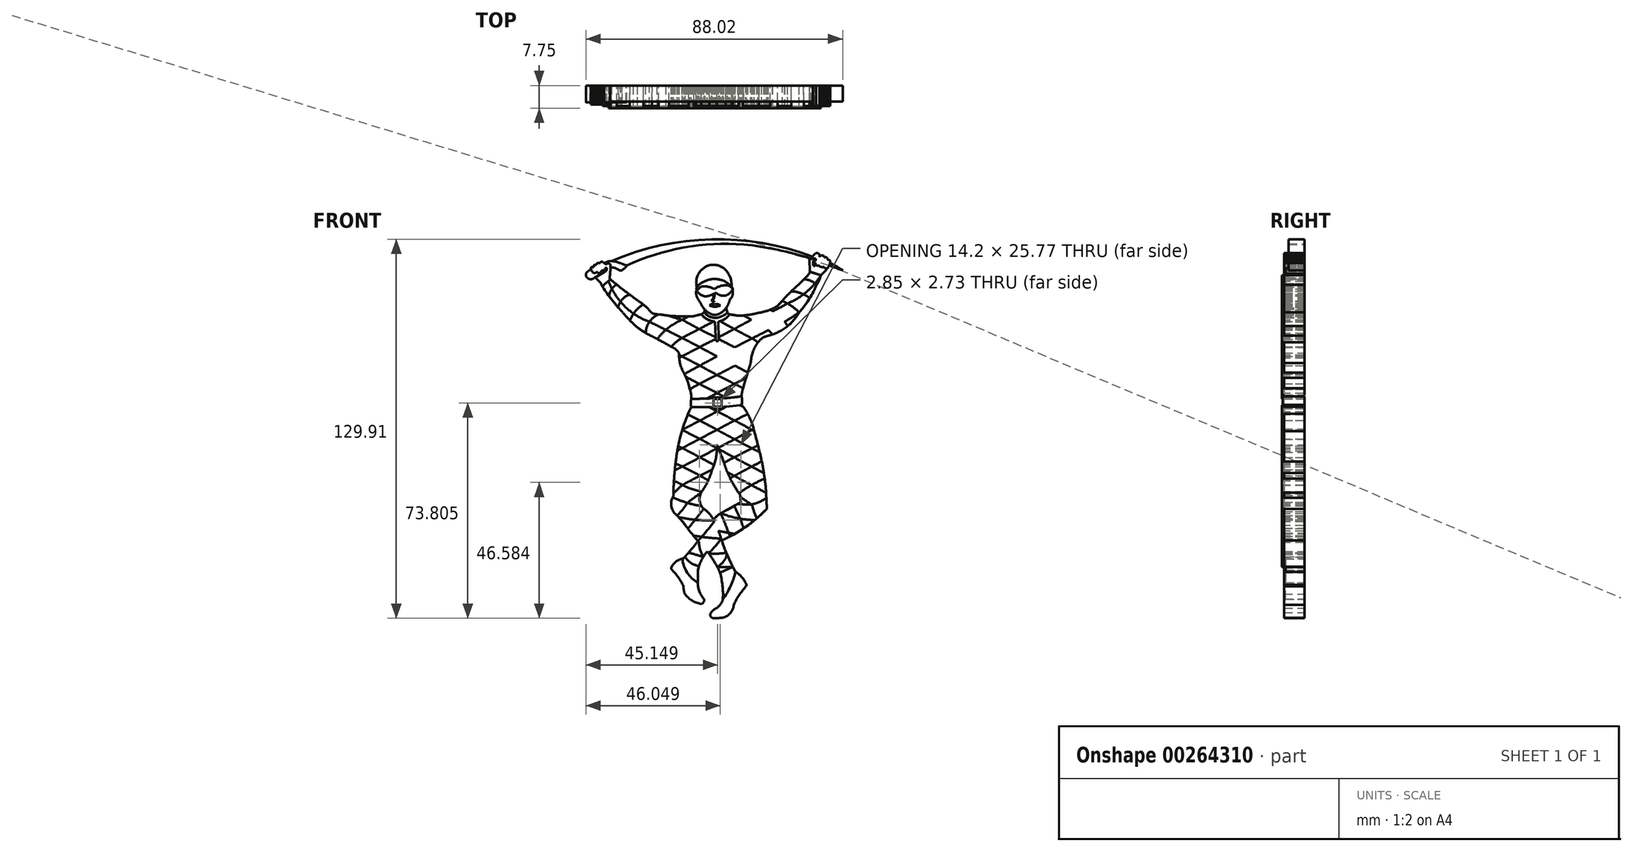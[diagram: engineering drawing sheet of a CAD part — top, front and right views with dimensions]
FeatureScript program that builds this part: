
annotation { "Feature Type Name" : "Feature", "Feature Type Description" : "" }
export const myFeature = defineFeature(function(context is Context, id is Id, definition is map)
    precondition{}
    {
        {
            var Q0;
            Q0=qCreatedBy(makeId("Front.planeOp"),FACE);
            var sketch = newSketch(context, id + "F0", { "sketchPlane" : qUnion([Q0])});
            skArc(sketch, "E0", {"start": v(-36.37, 62.76) * mm, "mid": v(-36.1, 65.18) * mm, "end": v(-36.02, 67.61) * mm});
            skLineSegment(sketch, "E1", {"start": v(-36.02, 67.61) * mm, "end": v(-36.67, 68.1) * mm});
            skArc(sketch, "E2", {"start": v(-36.67, 68.1) * mm, "mid": v(-37.17, 67.96) * mm, "end": v(-37.6, 67.68) * mm});
            skArc(sketch, "E3", {"start": v(-37.6, 67.68) * mm, "mid": v(-38.2, 68.15) * mm, "end": v(-38.83, 68.59) * mm});
            skArc(sketch, "E4", {"start": v(-38.83, 68.59) * mm, "mid": v(-39.14, 68.59) * mm, "end": v(-39.4, 68.45) * mm});
            skArc(sketch, "E5", {"start": v(-39.4, 68.45) * mm, "mid": v(-39.54, 68.3) * mm, "end": v(-39.58, 68.1) * mm});
            skArc(sketch, "E6", {"start": v(-39.58, 68.1) * mm, "mid": v(-39.84, 68.17) * mm, "end": v(-40.1, 68.2) * mm});
            skArc(sketch, "E7", {"start": v(-40.1, 68.2) * mm, "mid": v(-40.37, 68.18) * mm, "end": v(-40.6, 68.05) * mm});
            skArc(sketch, "E8", {"start": v(-40.6, 68.05) * mm, "mid": v(-40.8, 67.83) * mm, "end": v(-40.9, 67.56) * mm});
            skArc(sketch, "E9", {"start": v(-41.46, 67.56) * mm, "mid": v(-41.64, 67.48) * mm, "end": v(-41.77, 67.32) * mm});
            skArc(sketch, "E10", {"start": v(-41.77, 67.32) * mm, "mid": v(-41.81, 67.07) * mm, "end": v(-41.77, 66.82) * mm});
            skArc(sketch, "E11", {"start": v(-40.9, 67.56) * mm, "mid": v(-41.18, 67.58) * mm, "end": v(-41.46, 67.56) * mm});
            skArc(sketch, "E12", {"start": v(-41.77, 66.82) * mm, "mid": v(-42.13, 66.8) * mm, "end": v(-42.5, 66.74) * mm});
            skArc(sketch, "E13", {"start": v(-42.5, 66.74) * mm, "mid": v(-42.65, 66.64) * mm, "end": v(-42.73, 66.47) * mm});
            skArc(sketch, "E14", {"start": v(-42.73, 66.47) * mm, "mid": v(-42.46, 65.5) * mm, "end": v(-41.77, 64.76) * mm});
            skArc(sketch, "E15", {"start": v(-41.77, 64.76) * mm, "mid": v(-41.15, 64.8) * mm, "end": v(-40.64, 65.13) * mm});
            skArc(sketch, "E16", {"start": v(-40.64, 65.13) * mm, "mid": v(-40.38, 64.82) * mm, "end": v(-39.99, 64.68) * mm});
            skArc(sketch, "E17", {"start": v(-39.99, 64.68) * mm, "mid": v(-39.6, 64.72) * mm, "end": v(-39.3, 64.98) * mm});
            skArc(sketch, "E18", {"start": v(-39.3, 64.98) * mm, "mid": v(-39.18, 65.24) * mm, "end": v(-39.15, 65.53) * mm});
            skArc(sketch, "E19", {"start": v(-38.55, 65.59) * mm, "mid": v(-38.85, 65.56) * mm, "end": v(-39.15, 65.53) * mm});
            skArc(sketch, "E20", {"start": v(-38.55, 65.59) * mm, "mid": v(-38.33, 65.65) * mm, "end": v(-38.15, 65.79) * mm});
            skArc(sketch, "E21", {"start": v(-38.15, 65.79) * mm, "mid": v(-37.9, 66.12) * mm, "end": v(-37.76, 66.5) * mm});
            skArc(sketch, "E22", {"start": v(-37.28, 66.5) * mm, "mid": v(-37.52, 66.52) * mm, "end": v(-37.76, 66.5) * mm});
            skArc(sketch, "E23", {"start": v(-38.34, 65) * mm, "mid": v(-37.5, 65.52) * mm, "end": v(-37.28, 66.5) * mm});
            skLineSegment(sketch, "E24", {"start": v(-38.34, 65) * mm, "end": v(-41.2, 63.26) * mm});
            skLineSegment(sketch, "E25", {"start": v(-41.2, 63.26) * mm, "end": v(-39.25, 61.15) * mm});
            skArc(sketch, "E26", {"start": v(-39.25, 61.15) * mm, "mid": v(-39.04, 60.49) * mm, "end": v(-38.65, 59.91) * mm});
            skArc(sketch, "E27", {"start": v(-38.14, 60.8) * mm, "mid": v(-38.44, 60.38) * mm, "end": v(-38.65, 59.91) * mm});
            skLineSegment(sketch, "E28", {"start": v(-38.14, 60.8) * mm, "end": v(-36.03, 62.5) * mm});
            skArc(sketch, "E29", {"start": v(-36.03, 62.5) * mm, "mid": v(-36.17, 62.67) * mm, "end": v(-36.37, 62.76) * mm});
            skLineSegment(sketch, "E30", {"start": v(-3.7, 52.22) * mm, "end": v(-3.93, 51.3) * mm});
            skArc(sketch, "E31", {"start": v(-3.93, 51.3) * mm, "mid": v(-2.81, 50.2) * mm, "end": v(-1.39, 49.54) * mm});
            skArc(sketch, "E32", {"start": v(-1.39, 49.54) * mm, "mid": v(0.04, 49.34) * mm, "end": v(1.46, 49.64) * mm});
            skArc(sketch, "E33", {"start": v(1.46, 49.64) * mm, "mid": v(2.82, 50.24) * mm, "end": v(4.06, 51.06) * mm});
            skLineSegment(sketch, "E34", {"start": v(3.58, 52.8) * mm, "end": v(4.06, 51.06) * mm});
            skArc(sketch, "E35", {"start": v(-3.7, 52.22) * mm, "mid": v(-2.6, 51.2) * mm, "end": v(-1.23, 50.54) * mm});
            skArc(sketch, "E36", {"start": v(-1.23, 50.54) * mm, "mid": v(-0.11, 50.37) * mm, "end": v(0.99, 50.62) * mm});
            skArc(sketch, "E37", {"start": v(0.99, 50.62) * mm, "mid": v(2.44, 51.52) * mm, "end": v(3.58, 52.8) * mm});
            skLineSegment(sketch, "E38", {"start": v(32.12, 69.37) * mm, "end": v(32.24, 65.2) * mm});
            skLineSegment(sketch, "E39", {"start": v(32.24, 65.2) * mm, "end": v(36.08, 63.91) * mm});
            skArc(sketch, "E40", {"start": v(36.7, 64.53) * mm, "mid": v(36.38, 64.23) * mm, "end": v(36.08, 63.91) * mm});
            skArc(sketch, "E41", {"start": v(36.7, 64.53) * mm, "mid": v(37.54, 65.4) * mm, "end": v(38.3, 66.32) * mm});
            skArc(sketch, "E42", {"start": v(37.73, 66.32) * mm, "mid": v(38.02, 66.3) * mm, "end": v(38.3, 66.32) * mm});
            skArc(sketch, "E43", {"start": v(37.06, 66.85) * mm, "mid": v(37.33, 66.5) * mm, "end": v(37.73, 66.32) * mm});
            skArc(sketch, "E44", {"start": v(35.98, 66.85) * mm, "mid": v(36.52, 66.8) * mm, "end": v(37.06, 66.85) * mm});
            skArc(sketch, "E45", {"start": v(35.56, 67.22) * mm, "mid": v(35.72, 66.98) * mm, "end": v(35.98, 66.85) * mm});
            skArc(sketch, "E46", {"start": v(34.59, 67.38) * mm, "mid": v(35.06, 67.24) * mm, "end": v(35.56, 67.22) * mm});
            skArc(sketch, "E47", {"start": v(34.17, 67.88) * mm, "mid": v(34.32, 67.58) * mm, "end": v(34.59, 67.38) * mm});
            skArc(sketch, "E48", {"start": v(34.17, 68.32) * mm, "mid": v(34.14, 68.1) * mm, "end": v(34.17, 67.88) * mm});
            skArc(sketch, "E49", {"start": v(32.75, 69.71) * mm, "mid": v(32.4, 69.6) * mm, "end": v(32.12, 69.37) * mm});
            skLineSegment(sketch, "E50", {"start": v(32.75, 69.71) * mm, "end": v(34.26, 69.71) * mm});
            skArc(sketch, "E51", {"start": v(34.26, 69.18) * mm, "mid": v(34.35, 69.45) * mm, "end": v(34.26, 69.71) * mm});
            skArc(sketch, "E52", {"start": v(33.47, 68.74) * mm, "mid": v(33.91, 68.89) * mm, "end": v(34.26, 69.18) * mm});
            skLineSegment(sketch, "E53", {"start": v(33.47, 68.74) * mm, "end": v(33.47, 67.5) * mm});
            skArc(sketch, "E54", {"start": v(33.47, 67.5) * mm, "mid": v(33.54, 67.3) * mm, "end": v(33.72, 67.2) * mm});
            skArc(sketch, "E55", {"start": v(33.72, 67.2) * mm, "mid": v(33.9, 67.2) * mm, "end": v(34.01, 67.34) * mm});
            skArc(sketch, "E56", {"start": v(34.01, 67.34) * mm, "mid": v(33.99, 67.52) * mm, "end": v(33.88, 67.66) * mm});
            skArc(sketch, "E57", {"start": v(33.88, 68.3) * mm, "mid": v(33.84, 67.98) * mm, "end": v(33.88, 67.66) * mm});
            skArc(sketch, "E58", {"start": v(34.17, 68.32) * mm, "mid": v(34.02, 68.32) * mm, "end": v(33.88, 68.3) * mm});
            skArc(sketch, "E59", {"start": v(-10.4, -32.58) * mm, "mid": v(-8.42, -34.73) * mm, "end": v(-5.68, -35.77) * mm});
            skArc(sketch, "E60", {"start": v(-11.4, -33.28) * mm, "mid": v(-9.76, -38) * mm, "end": v(-6.12, -41.43) * mm});
            skArc(sketch, "E61", {"start": v(-6.12, -41.43) * mm, "mid": v(-6.03, -39.3) * mm, "end": v(-6.04, -37.17) * mm});
            skLineSegment(sketch, "E62", {"start": v(-6.04, -37.17) * mm, "end": v(-5.68, -35.77) * mm});
            skLineSegment(sketch, "E63", {"start": v(-11.4, -33.28) * mm, "end": v(-10.4, -32.58) * mm});
            skArc(sketch, "E64", {"start": v(2.49, -47.2) * mm, "mid": v(2.36, -42.53) * mm, "end": v(1.48, -37.94) * mm});
            skArc(sketch, "E65", {"start": v(2.49, -47.2) * mm, "mid": v(5.15, -42.7) * mm, "end": v(6.82, -37.74) * mm});
            skLineSegment(sketch, "E66", {"start": v(1.48, -37.94) * mm, "end": v(5.96, -36.05) * mm});
            skLineSegment(sketch, "E67", {"start": v(5.96, -36.05) * mm, "end": v(6.82, -37.74) * mm});
            skSolve(sketch);
        }
        {
            var Q0;
            Q0=qCreatedBy(makeId("Front.planeOp"),FACE);
            var sketch = newSketch(context, id + "F1", { "sketchPlane" : qUnion([Q0])});
            skArc(sketch, "E68", {"start": v(34.17, 68.32) * mm, "mid": v(34.14, 68.1) * mm, "end": v(34.18, 67.88) * mm});
            skArc(sketch, "E69", {"start": v(34.18, 67.88) * mm, "mid": v(34.32, 67.58) * mm, "end": v(34.59, 67.39) * mm});
            skArc(sketch, "E70", {"start": v(34.59, 67.39) * mm, "mid": v(35.06, 67.25) * mm, "end": v(35.55, 67.23) * mm});
            skArc(sketch, "E71", {"start": v(35.55, 67.23) * mm, "mid": v(35.72, 66.98) * mm, "end": v(35.99, 66.85) * mm});
            skArc(sketch, "E72", {"start": v(35.99, 66.85) * mm, "mid": v(36.52, 66.8) * mm, "end": v(37.06, 66.85) * mm});
            skArc(sketch, "E73", {"start": v(37.06, 66.85) * mm, "mid": v(37.33, 66.5) * mm, "end": v(37.73, 66.32) * mm});
            skArc(sketch, "E74", {"start": v(37.73, 66.32) * mm, "mid": v(38.02, 66.3) * mm, "end": v(38.3, 66.32) * mm});
            skArc(sketch, "E75", {"start": v(33.48, 68.47) * mm, "mid": v(33.8, 68.33) * mm, "end": v(34.17, 68.32) * mm});
            skArc(sketch, "E76", {"start": v(38.3, 66.32) * mm, "mid": v(38.86, 67.2) * mm, "end": v(39.2, 68.2) * mm});
            skArc(sketch, "E77", {"start": v(39.2, 68.2) * mm, "mid": v(39.27, 68.59) * mm, "end": v(39.2, 68.98) * mm});
            skArc(sketch, "E78", {"start": v(39.2, 68.98) * mm, "mid": v(39.02, 69.14) * mm, "end": v(38.8, 69.25) * mm});
            skArc(sketch, "E79", {"start": v(38.8, 69.25) * mm, "mid": v(38.55, 69.29) * mm, "end": v(38.3, 69.25) * mm});
            skArc(sketch, "E80", {"start": v(38.3, 69.25) * mm, "mid": v(38.35, 69.5) * mm, "end": v(38.3, 69.76) * mm});
            skArc(sketch, "E81", {"start": v(38.3, 69.76) * mm, "mid": v(38.14, 70) * mm, "end": v(37.9, 70.14) * mm});
            skArc(sketch, "E82", {"start": v(37.9, 70.14) * mm, "mid": v(37.59, 70.14) * mm, "end": v(37.28, 70.06) * mm});
            skArc(sketch, "E83", {"start": v(34.46, 71.56) * mm, "mid": v(33.88, 71.14) * mm, "end": v(33.43, 70.59) * mm});
            skArc(sketch, "E84", {"start": v(35.55, 71.17) * mm, "mid": v(35.06, 71.53) * mm, "end": v(34.46, 71.56) * mm});
            skArc(sketch, "E85", {"start": v(33.43, 70.59) * mm, "mid": v(33.12, 70.16) * mm, "end": v(32.87, 69.71) * mm});
            skArc(sketch, "E86", {"start": v(34.27, 69.18) * mm, "mid": v(34.35, 69.45) * mm, "end": v(34.26, 69.71) * mm});
            skArc(sketch, "E87", {"start": v(33.47, 68.75) * mm, "mid": v(33.91, 68.89) * mm, "end": v(34.27, 69.18) * mm});
            skLineSegment(sketch, "E88", {"start": v(33.47, 68.75) * mm, "end": v(33.48, 68.47) * mm});
            skLineSegment(sketch, "E89", {"start": v(32.87, 69.71) * mm, "end": v(34.26, 69.71) * mm});
            skArc(sketch, "E90", {"start": v(35.55, 70.31) * mm, "mid": v(35.6, 70.74) * mm, "end": v(35.55, 71.17) * mm});
            skArc(sketch, "E91", {"start": v(36.26, 70.76) * mm, "mid": v(35.88, 70.59) * mm, "end": v(35.55, 70.31) * mm});
            skArc(sketch, "E92", {"start": v(37.11, 70.59) * mm, "mid": v(36.7, 70.74) * mm, "end": v(36.26, 70.76) * mm});
            skArc(sketch, "E93", {"start": v(37.28, 70.06) * mm, "mid": v(37.25, 70.34) * mm, "end": v(37.11, 70.59) * mm});
            skArc(sketch, "E94", {"start": v(-3.7, 52.23) * mm, "mid": v(-2.6, 51.2) * mm, "end": v(-1.23, 50.54) * mm});
            skArc(sketch, "E95", {"start": v(-1.23, 50.54) * mm, "mid": v(-0.11, 50.38) * mm, "end": v(1, 50.62) * mm});
            skArc(sketch, "E96", {"start": v(1, 50.62) * mm, "mid": v(2.44, 51.52) * mm, "end": v(3.57, 52.8) * mm});
            skArc(sketch, "E97", {"start": v(3.57, 52.8) * mm, "mid": v(4.44, 54.19) * mm, "end": v(4.91, 55.77) * mm});
            skArc(sketch, "E98", {"start": v(4.91, 55.77) * mm, "mid": v(5.55, 56.45) * mm, "end": v(5.85, 57.33) * mm});
            skArc(sketch, "E99", {"start": v(5.85, 57.33) * mm, "mid": v(5.91, 58.44) * mm, "end": v(5.85, 59.54) * mm});
            skArc(sketch, "E100", {"start": v(5.85, 59.54) * mm, "mid": v(5.68, 59.75) * mm, "end": v(5.46, 59.9) * mm});
            skArc(sketch, "E101", {"start": v(5.46, 59.9) * mm, "mid": v(3.62, 61.6) * mm, "end": v(1.28, 62.5) * mm});
            skArc(sketch, "E102", {"start": v(1.28, 62.5) * mm, "mid": v(-0.42, 62.68) * mm, "end": v(-2.12, 62.5) * mm});
            skArc(sketch, "E103", {"start": v(-2.12, 62.5) * mm, "mid": v(-4.49, 61.54) * mm, "end": v(-6.45, 59.9) * mm});
            skArc(sketch, "E104", {"start": v(-6.45, 59.9) * mm, "mid": v(-6.53, 59.3) * mm, "end": v(-6.45, 58.69) * mm});
            skArc(sketch, "E105", {"start": v(-6.45, 58.69) * mm, "mid": v(-6.62, 58.63) * mm, "end": v(-6.73, 58.5) * mm});
            skArc(sketch, "E106", {"start": v(-6.73, 58.5) * mm, "mid": v(-6.4, 56.54) * mm, "end": v(-5.38, 54.84) * mm});
            skArc(sketch, "E107", {"start": v(-5.38, 54.84) * mm, "mid": v(-4.67, 53.45) * mm, "end": v(-3.7, 52.23) * mm});
            skSolve(sketch);
        }
        {
            var Q0;
            Q0=qCreatedBy(makeId("Front.planeOp"),FACE);
            var sketch = newSketch(context, id + "F2", { "sketchPlane" : qUnion([Q0])});
            skArc(sketch, "E108", {"start": v(-38.15, 60.8) * mm, "mid": v(-38.45, 60.39) * mm, "end": v(-38.65, 59.92) * mm});
            skLineSegment(sketch, "E109", {"start": v(-38.15, 60.8) * mm, "end": v(-36, 62.53) * mm});
            skArc(sketch, "E110", {"start": v(-36, 62.53) * mm, "mid": v(-30.5, 58.1) * mm, "end": v(-24.76, 53.97) * mm});
            skArc(sketch, "E111", {"start": v(-21.76, 50.88) * mm, "mid": v(-23.2, 52.48) * mm, "end": v(-24.76, 53.97) * mm});
            skArc(sketch, "E112", {"start": v(-21.76, 50.88) * mm, "mid": v(-14.63, 49.98) * mm, "end": v(-7.45, 49.93) * mm});
            skArc(sketch, "E113", {"start": v(-4.86, 50.59) * mm, "mid": v(-6.16, 50.28) * mm, "end": v(-7.45, 49.93) * mm});
            skArc(sketch, "E114", {"start": v(-4.86, 50.59) * mm, "mid": v(-4.37, 50.92) * mm, "end": v(-3.92, 51.3) * mm});
            skArc(sketch, "E115", {"start": v(-3.92, 51.3) * mm, "mid": v(-2.82, 50.2) * mm, "end": v(-1.4, 49.56) * mm});
            skArc(sketch, "E116", {"start": v(-1.4, 49.56) * mm, "mid": v(0.04, 49.34) * mm, "end": v(1.46, 49.64) * mm});
            skArc(sketch, "E117", {"start": v(1.46, 49.64) * mm, "mid": v(2.82, 50.24) * mm, "end": v(4.06, 51.06) * mm});
            skArc(sketch, "E118", {"start": v(4.06, 51.06) * mm, "mid": v(4.28, 50.8) * mm, "end": v(4.53, 50.59) * mm});
            skArc(sketch, "E119", {"start": v(14.9, 51.11) * mm, "mid": v(18.2, 51.95) * mm, "end": v(21.24, 53.44) * mm});
            skArc(sketch, "E120", {"start": v(25.94, 58.47) * mm, "mid": v(23.55, 55.99) * mm, "end": v(21.24, 53.44) * mm});
            skArc(sketch, "E121", {"start": v(25.94, 58.47) * mm, "mid": v(29.17, 61.45) * mm, "end": v(32.18, 64.66) * mm});
            skArc(sketch, "E122", {"start": v(32.18, 64.66) * mm, "mid": v(32.24, 64.92) * mm, "end": v(32.24, 65.2) * mm});
            skArc(sketch, "E123", {"start": v(34.57, 60.7) * mm, "mid": v(35.48, 62.23) * mm, "end": v(36.07, 63.91) * mm});
            skArc(sketch, "E124", {"start": v(28.62, 51.25) * mm, "mid": v(32.02, 55.7) * mm, "end": v(34.57, 60.7) * mm});
            skArc(sketch, "E125", {"start": v(24.7, 46.53) * mm, "mid": v(26.87, 48.72) * mm, "end": v(28.62, 51.25) * mm});
            skArc(sketch, "E126", {"start": v(18.04, 43.23) * mm, "mid": v(21.55, 44.52) * mm, "end": v(24.7, 46.53) * mm});
            skArc(sketch, "E127", {"start": v(18.04, 43.23) * mm, "mid": v(16.08, 42.44) * mm, "end": v(14.53, 41) * mm});
            skArc(sketch, "E128", {"start": v(14.53, 41) * mm, "mid": v(12.75, 37.6) * mm, "end": v(12.02, 33.84) * mm});
            skArc(sketch, "E129", {"start": v(12.02, 33.84) * mm, "mid": v(10.66, 29.55) * mm, "end": v(9.44, 25.23) * mm});
            skLineSegment(sketch, "E130", {"start": v(2.72, 21.75) * mm, "end": v(2.72, 22.1) * mm});
            skLineSegment(sketch, "E131", {"start": v(2.72, 22.1) * mm, "end": v(-1.38, 22.1) * mm});
            skLineSegment(sketch, "E132", {"start": v(-1.38, 22.1) * mm, "end": v(-1.38, 21.75) * mm});
            skArc(sketch, "E133", {"start": v(-8.35, 21.5) * mm, "mid": v(-4.86, 21.55) * mm, "end": v(-1.38, 21.75) * mm});
            skArc(sketch, "E134", {"start": v(-8.37, 18.79) * mm, "mid": v(-4.87, 18.69) * mm, "end": v(-1.38, 18.82) * mm});
            skLineSegment(sketch, "E135", {"start": v(-1.38, 18.82) * mm, "end": v(-1.38, 18.28) * mm});
            skLineSegment(sketch, "E136", {"start": v(-1.38, 18.28) * mm, "end": v(2.72, 18.28) * mm});
            skLineSegment(sketch, "E137", {"start": v(2.72, 18.28) * mm, "end": v(2.72, 18.82) * mm});
            skArc(sketch, "E138", {"start": v(2.72, 18.82) * mm, "mid": v(5.83, 19.1) * mm, "end": v(8.92, 19.51) * mm});
            skArc(sketch, "E139", {"start": v(9.44, 25.23) * mm, "mid": v(9.05, 23.86) * mm, "end": v(8.92, 22.43) * mm});
            skArc(sketch, "E140", {"start": v(2.72, 21.75) * mm, "mid": v(5.83, 22) * mm, "end": v(8.92, 22.43) * mm});
            skArc(sketch, "E141", {"start": v(-8.35, 21.5) * mm, "mid": v(-8.4, 23.22) * mm, "end": v(-8.85, 24.9) * mm});
            skArc(sketch, "E142", {"start": v(-8.85, 24.9) * mm, "mid": v(-9.58, 27.56) * mm, "end": v(-10.7, 30.1) * mm});
            skArc(sketch, "E143", {"start": v(-12.5, 37.25) * mm, "mid": v(-12.12, 33.54) * mm, "end": v(-10.7, 30.1) * mm});
            skArc(sketch, "E144", {"start": v(-12.5, 37.25) * mm, "mid": v(-13.65, 38.51) * mm, "end": v(-15.1, 39.43) * mm});
            skArc(sketch, "E145", {"start": v(-15.1, 39.43) * mm, "mid": v(-18.37, 41.25) * mm, "end": v(-21.7, 42.97) * mm});
            skArc(sketch, "E146", {"start": v(-26.74, 46.02) * mm, "mid": v(-24.3, 44.37) * mm, "end": v(-21.7, 42.97) * mm});
            skArc(sketch, "E147", {"start": v(-32.1, 51.5) * mm, "mid": v(-29.54, 48.64) * mm, "end": v(-26.74, 46.02) * mm});
            skArc(sketch, "E148", {"start": v(-38.65, 59.92) * mm, "mid": v(-35.58, 55.55) * mm, "end": v(-32.1, 51.5) * mm});
            skArc(sketch, "E149", {"start": v(7.97, 50.06) * mm, "mid": v(6.25, 50.35) * mm, "end": v(4.53, 50.59) * mm});
            skArc(sketch, "E150", {"start": v(7.97, 50.06) * mm, "mid": v(11.47, 50.4) * mm, "end": v(14.9, 51.11) * mm});
            skArc(sketch, "E151", {"start": v(-8.37, 18.79) * mm, "mid": v(-11.24, 11.55) * mm, "end": v(-13.08, 3.98) * mm});
            skArc(sketch, "E152", {"start": v(-13.08, 3.98) * mm, "mid": v(-14.08, -3.9) * mm, "end": v(-14.47, -11.83) * mm});
            skArc(sketch, "E153", {"start": v(-14.47, -11.83) * mm, "mid": v(-15.1, -15.37) * mm, "end": v(-13.2, -18.43) * mm});
            skArc(sketch, "E154", {"start": v(-10.37, -21.76) * mm, "mid": v(-11.73, -20.04) * mm, "end": v(-13.2, -18.43) * mm});
            skArc(sketch, "E155", {"start": v(-10.37, -21.76) * mm, "mid": v(-8.27, -24.51) * mm, "end": v(-6.08, -27.2) * mm});
            skArc(sketch, "E156", {"start": v(1.51, -37.97) * mm, "mid": v(-1.78, -32.23) * mm, "end": v(-6.08, -27.2) * mm});
            skLineSegment(sketch, "E157", {"start": v(1.51, -37.97) * mm, "end": v(5.94, -36.04) * mm});
            skArc(sketch, "E158", {"start": v(2.1, -26.95) * mm, "mid": v(3.8, -31.58) * mm, "end": v(5.94, -36.04) * mm});
            skArc(sketch, "E159", {"start": v(2.1, -26.95) * mm, "mid": v(0.87, -23.47) * mm, "end": v(-0.63, -20.1) * mm});
            skArc(sketch, "E160", {"start": v(-0.63, -20.1) * mm, "mid": v(-2.07, -17.9) * mm, "end": v(-4.05, -16.17) * mm});
            skArc(sketch, "E161", {"start": v(-5, -10.63) * mm, "mid": v(-5.45, -13.56) * mm, "end": v(-4.05, -16.17) * mm});
            skArc(sketch, "E162", {"start": v(-5, -10.63) * mm, "mid": v(-2.76, -6.8) * mm, "end": v(-1.16, -2.67) * mm});
            skArc(sketch, "E163", {"start": v(-1.16, -2.67) * mm, "mid": v(0.16, 1.49) * mm, "end": v(0.47, 5.84) * mm});
            skArc(sketch, "E164", {"start": v(3.66, -2.67) * mm, "mid": v(2.15, 1.62) * mm, "end": v(0.47, 5.84) * mm});
            skArc(sketch, "E165", {"start": v(3.66, -2.67) * mm, "mid": v(5.82, -7.18) * mm, "end": v(8.47, -11.42) * mm});
            skArc(sketch, "E166", {"start": v(8.47, -11.42) * mm, "mid": v(8.52, -12.64) * mm, "end": v(8.68, -13.85) * mm});
            skArc(sketch, "E167", {"start": v(13.22, 10.53) * mm, "mid": v(11.59, 15.27) * mm, "end": v(8.92, 19.51) * mm});
            skArc(sketch, "E168", {"start": v(15.83, 0.13) * mm, "mid": v(14.6, 5.35) * mm, "end": v(13.22, 10.53) * mm});
            skArc(sketch, "E169", {"start": v(17.5, -16.17) * mm, "mid": v(17.05, -7.98) * mm, "end": v(15.83, 0.13) * mm});
            skArc(sketch, "E170", {"start": v(2.1, -26.95) * mm, "mid": v(10.35, -22.35) * mm, "end": v(17.5, -16.17) * mm});
            skArc(sketch, "E171", {"start": v(2.85, -17.1) * mm, "mid": v(0.88, -18.28) * mm, "end": v(-0.71, -19.93) * mm});
            skArc(sketch, "E172", {"start": v(8.68, -13.85) * mm, "mid": v(5.76, -15.47) * mm, "end": v(2.85, -17.1) * mm});
            skArc(sketch, "E173", {"start": v(-10.49, -32.5) * mm, "mid": v(-8.46, -34.72) * mm, "end": v(-5.64, -35.76) * mm});
            skArc(sketch, "E174", {"start": v(-2.86, -30.78) * mm, "mid": v(-4.53, -33.12) * mm, "end": v(-5.64, -35.76) * mm});
            skArc(sketch, "E175", {"start": v(-10.49, -32.5) * mm, "mid": v(-8.2, -29.91) * mm, "end": v(-6.08, -27.2) * mm});
            skLineSegment(sketch, "E176", {"start": v(32.24, 65.2) * mm, "end": v(36.07, 63.91) * mm});
            skArc(sketch, "E177", {"start": v(-11.4, -33.23) * mm, "mid": v(-9.78, -37.97) * mm, "end": v(-6.13, -41.4) * mm});
            skArc(sketch, "E178", {"start": v(-11.4, -33.23) * mm, "mid": v(-13.69, -34.33) * mm, "end": v(-15.19, -36.38) * mm});
            skArc(sketch, "E179", {"start": v(-15.19, -36.38) * mm, "mid": v(-15.13, -36.83) * mm, "end": v(-14.87, -37.19) * mm});
            skArc(sketch, "E180", {"start": v(-10.96, -42.73) * mm, "mid": v(-12.68, -39.8) * mm, "end": v(-14.87, -37.19) * mm});
            skArc(sketch, "E181", {"start": v(-10.96, -42.73) * mm, "mid": v(-10.9, -44.06) * mm, "end": v(-10.52, -45.33) * mm});
            skArc(sketch, "E182", {"start": v(-10.52, -45.33) * mm, "mid": v(-8.03, -47.6) * mm, "end": v(-4.87, -48.77) * mm});
            skArc(sketch, "E183", {"start": v(-4.87, -48.77) * mm, "mid": v(-4.1, -48.1) * mm, "end": v(-3.98, -47.1) * mm});
            skArc(sketch, "E184", {"start": v(-6.13, -41.4) * mm, "mid": v(-5.55, -44.44) * mm, "end": v(-3.98, -47.1) * mm});
            skArc(sketch, "E185", {"start": v(2.49, -47.2) * mm, "mid": v(5.12, -42.68) * mm, "end": v(6.8, -37.74) * mm});
            skArc(sketch, "E186", {"start": v(10.57, -42.22) * mm, "mid": v(9.08, -39.64) * mm, "end": v(6.8, -37.74) * mm});
            skArc(sketch, "E187", {"start": v(10.38, -42.73) * mm, "mid": v(10.53, -42.5) * mm, "end": v(10.57, -42.22) * mm});
            skArc(sketch, "E188", {"start": v(10.38, -42.73) * mm, "mid": v(8.06, -45.73) * mm, "end": v(6.25, -49.06) * mm});
            skArc(sketch, "E189", {"start": v(1.34, -53.57) * mm, "mid": v(4.67, -52.28) * mm, "end": v(6.25, -49.06) * mm});
            skArc(sketch, "E190", {"start": v(-1.1, -53.57) * mm, "mid": v(0.12, -53.63) * mm, "end": v(1.34, -53.57) * mm});
            skArc(sketch, "E191", {"start": v(-1.57, -51.8) * mm, "mid": v(-1.78, -52.8) * mm, "end": v(-1.1, -53.57) * mm});
            skArc(sketch, "E192", {"start": v(0.36, -50.19) * mm, "mid": v(-0.72, -50.85) * mm, "end": v(-1.57, -51.8) * mm});
            skArc(sketch, "E193", {"start": v(0.36, -50.19) * mm, "mid": v(1.66, -48.86) * mm, "end": v(2.49, -47.2) * mm});
            skArc(sketch, "E194", {"start": v(-2.1, 62.5) * mm, "mid": v(-4.47, 61.54) * mm, "end": v(-6.46, 59.93) * mm});
            skArc(sketch, "E195", {"start": v(1.28, 62.5) * mm, "mid": v(-0.4, 62.68) * mm, "end": v(-2.1, 62.5) * mm});
            skArc(sketch, "E196", {"start": v(5.46, 59.9) * mm, "mid": v(3.62, 61.6) * mm, "end": v(1.28, 62.5) * mm});
            skArc(sketch, "E197", {"start": v(5.46, 59.9) * mm, "mid": v(5.07, 63.03) * mm, "end": v(3.44, 65.73) * mm});
            skArc(sketch, "E198", {"start": v(3.44, 65.73) * mm, "mid": v(2.02, 66.82) * mm, "end": v(0.36, 67.44) * mm});
            skArc(sketch, "E199", {"start": v(0.36, 67.44) * mm, "mid": v(-0.87, 67.53) * mm, "end": v(-2.1, 67.44) * mm});
            skArc(sketch, "E200", {"start": v(-2.1, 67.44) * mm, "mid": v(-3.6, 66.78) * mm, "end": v(-4.87, 65.73) * mm});
            skArc(sketch, "E201", {"start": v(-4.87, 65.73) * mm, "mid": v(-6.42, 63.04) * mm, "end": v(-6.46, 59.93) * mm});
            skArc(sketch, "E202", {"start": v(-4.63, 60.18) * mm, "mid": v(-5.61, 59.53) * mm, "end": v(-6.46, 58.71) * mm});
            skArc(sketch, "E203", {"start": v(-0.43, 59.2) * mm, "mid": v(-2.45, 60.01) * mm, "end": v(-4.63, 60.18) * mm});
            skArc(sketch, "E204", {"start": v(4.05, 60.5) * mm, "mid": v(1.7, 60.27) * mm, "end": v(-0.43, 59.2) * mm});
            skArc(sketch, "E205", {"start": v(5.91, 59.33) * mm, "mid": v(5.06, 60.03) * mm, "end": v(4.05, 60.5) * mm});
            skArc(sketch, "E206", {"start": v(3.42, 56.98) * mm, "mid": v(4.89, 57.92) * mm, "end": v(5.91, 59.33) * mm});
            skArc(sketch, "E207", {"start": v(-3.55, 56.73) * mm, "mid": v(-1.86, 57.05) * mm, "end": v(-0.33, 57.85) * mm});
            skArc(sketch, "E208", {"start": v(-6.46, 58.71) * mm, "mid": v(-5.22, 57.4) * mm, "end": v(-3.55, 56.73) * mm});
            skArc(sketch, "E209", {"start": v(0.25, 57.85) * mm, "mid": v(1.74, 57.08) * mm, "end": v(3.42, 56.98) * mm});
            skArc(sketch, "E210", {"start": v(-0.33, 57.85) * mm, "mid": v(-0.04, 57.84) * mm, "end": v(0.25, 57.85) * mm});
            skArc(sketch, "E211", {"start": v(-0.22, 53.97) * mm, "mid": v(-1.21, 54.1) * mm, "end": v(-2.1, 53.65) * mm});
            skArc(sketch, "E212", {"start": v(1.67, 53.65) * mm, "mid": v(0.76, 54.04) * mm, "end": v(-0.22, 53.97) * mm});
            skArc(sketch, "E213", {"start": v(-2.1, 53.65) * mm, "mid": v(-0.21, 53.2) * mm, "end": v(1.67, 53.65) * mm});
            skArc(sketch, "E214", {"start": v(-1.2, 54.99) * mm, "mid": v(-0.85, 54.9) * mm, "end": v(-0.49, 54.88) * mm});
            skArc(sketch, "E215", {"start": v(-1.2, 55.62) * mm, "mid": v(-1.26, 55.3) * mm, "end": v(-1.2, 54.99) * mm});
            skArc(sketch, "E216", {"start": v(-1.2, 55.62) * mm, "mid": v(-0.98, 55.86) * mm, "end": v(-0.84, 56.16) * mm});
            skArc(sketch, "E217", {"start": v(-0.84, 56.16) * mm, "mid": v(-0.66, 56.9) * mm, "end": v(-0.63, 57.65) * mm});
            skArc(sketch, "E218", {"start": v(-0.49, 54.88) * mm, "mid": v(-0.45, 55) * mm, "end": v(-0.49, 55.12) * mm});
            skArc(sketch, "E219", {"start": v(-0.49, 55.12) * mm, "mid": v(-0.7, 55.13) * mm, "end": v(-0.9, 55.12) * mm});
            skArc(sketch, "E220", {"start": v(-0.9, 55.55) * mm, "mid": v(-0.98, 55.33) * mm, "end": v(-0.9, 55.12) * mm});
            skArc(sketch, "E221", {"start": v(-0.9, 55.55) * mm, "mid": v(-0.67, 55.84) * mm, "end": v(-0.49, 56.16) * mm});
            skArc(sketch, "E222", {"start": v(-0.49, 56.16) * mm, "mid": v(-0.38, 56.98) * mm, "end": v(-0.4, 57.81) * mm});
            skLineSegment(sketch, "E223", {"start": v(-0.78, 21.56) * mm, "end": v(2.13, 21.56) * mm});
            skLineSegment(sketch, "E224", {"start": v(2.13, 21.56) * mm, "end": v(2.13, 18.9) * mm});
            skLineSegment(sketch, "E225", {"start": v(2.13, 18.9) * mm, "end": v(-0.78, 18.9) * mm});
            skLineSegment(sketch, "E226", {"start": v(-0.78, 18.9) * mm, "end": v(-0.78, 21.56) * mm});
            skSolve(sketch);
        }
        {
            var Q0;
            Q0=qCreatedBy(makeId("Front.planeOp"),FACE);
            var sketch = newSketch(context, id + "F3", { "sketchPlane" : qUnion([Q0])});
            skArc(sketch, "E227", {"start": v(-38.34, 65) * mm, "mid": v(-37.48, 65.53) * mm, "end": v(-37.28, 66.52) * mm});
            skArc(sketch, "E228", {"start": v(-33.13, 65.73) * mm, "mid": v(-34.5, 66.47) * mm, "end": v(-36.04, 66.52) * mm});
            skArc(sketch, "E229", {"start": v(-33.13, 65.73) * mm, "mid": v(-32.55, 65.57) * mm, "end": v(-31.97, 65.73) * mm});
            skArc(sketch, "E230", {"start": v(-31.97, 65.73) * mm, "mid": v(-31.17, 66.44) * mm, "end": v(-30.39, 67.17) * mm});
            skArc(sketch, "E231", {"start": v(-30.39, 67.17) * mm, "mid": v(-33.18, 68.32) * mm, "end": v(-36.16, 68.88) * mm});
            skArc(sketch, "E232", {"start": v(-36.16, 68.88) * mm, "mid": v(-37.18, 68.56) * mm, "end": v(-38.14, 68.1) * mm});
            skArc(sketch, "E233", {"start": v(-42.65, 65.94) * mm, "mid": v(-43.62, 65.41) * mm, "end": v(-44.42, 64.65) * mm});
            skArc(sketch, "E234", {"start": v(-44.42, 64.65) * mm, "mid": v(-44.2, 63.33) * mm, "end": v(-43.06, 62.62) * mm});
            skArc(sketch, "E235", {"start": v(-43.06, 62.62) * mm, "mid": v(-42.28, 62.66) * mm, "end": v(-41.6, 63.03) * mm});
            skLineSegment(sketch, "E236", {"start": v(-38.34, 65) * mm, "end": v(-41.6, 63.03) * mm});
            skArc(sketch, "E237", {"start": v(-42.65, 65.94) * mm, "mid": v(-42.31, 65.27) * mm, "end": v(-41.77, 64.76) * mm});
            skArc(sketch, "E238", {"start": v(-41.77, 64.76) * mm, "mid": v(-41.16, 64.8) * mm, "end": v(-40.65, 65.13) * mm});
            skArc(sketch, "E239", {"start": v(-40.65, 65.13) * mm, "mid": v(-40.38, 64.83) * mm, "end": v(-40, 64.69) * mm});
            skArc(sketch, "E240", {"start": v(-40, 64.69) * mm, "mid": v(-39.6, 64.72) * mm, "end": v(-39.3, 64.98) * mm});
            skArc(sketch, "E241", {"start": v(-39.3, 64.98) * mm, "mid": v(-39.18, 65.24) * mm, "end": v(-39.15, 65.53) * mm});
            skArc(sketch, "E242", {"start": v(-39.15, 65.53) * mm, "mid": v(-38.85, 65.55) * mm, "end": v(-38.54, 65.58) * mm});
            skArc(sketch, "E243", {"start": v(-38.54, 65.58) * mm, "mid": v(-38.33, 65.65) * mm, "end": v(-38.15, 65.79) * mm});
            skArc(sketch, "E244", {"start": v(-38.15, 65.79) * mm, "mid": v(-37.9, 66.11) * mm, "end": v(-37.76, 66.5) * mm});
            skArc(sketch, "E245", {"start": v(-37.28, 66.52) * mm, "mid": v(-37.52, 66.52) * mm, "end": v(-37.76, 66.5) * mm});
            skArc(sketch, "E246", {"start": v(-36.67, 68.1) * mm, "mid": v(-37.17, 67.95) * mm, "end": v(-37.6, 67.68) * mm});
            skLineSegment(sketch, "E247", {"start": v(-37.6, 67.68) * mm, "end": v(-38.14, 68.1) * mm});
            skLineSegment(sketch, "E248", {"start": v(-36.67, 68.1) * mm, "end": v(-36.02, 67.62) * mm});
            skLineSegment(sketch, "E249", {"start": v(-36.02, 67.62) * mm, "end": v(-36.04, 66.52) * mm});
            skSolve(sketch);
        }
        {
            var Q0;
            Q0=qCreatedBy(makeId("Front.planeOp"),FACE);
            var sketch = newSketch(context, id + "F4", { "sketchPlane" : qUnion([Q0])});
            skArc(sketch, "E250", {"start": v(-30.64, 67.29) * mm, "mid": v(-33.14, 68.29) * mm, "end": v(-35.78, 68.83) * mm});
            skArc(sketch, "E251", {"start": v(33.26, 70.37) * mm, "mid": v(-1.4, 76.26) * mm, "end": v(-35.78, 68.83) * mm});
            skArc(sketch, "E252", {"start": v(9.62, 74.54) * mm, "mid": v(-10.97, 73.46) * mm, "end": v(-30.64, 67.29) * mm});
            skArc(sketch, "E253", {"start": v(32.61, 69.68) * mm, "mid": v(21.24, 72.69) * mm, "end": v(9.62, 74.54) * mm});
            skArc(sketch, "E254", {"start": v(43.55, 65.64) * mm, "mid": v(41.4, 66.99) * mm, "end": v(39.2, 68.2) * mm});
            skArc(sketch, "E255", {"start": v(32.87, 69.71) * mm, "mid": v(32.74, 69.7) * mm, "end": v(32.61, 69.68) * mm});
            skArc(sketch, "E256", {"start": v(33.26, 70.37) * mm, "mid": v(33.05, 70.05) * mm, "end": v(32.87, 69.71) * mm});
            skArc(sketch, "E257", {"start": v(38.91, 67.32) * mm, "mid": v(39.08, 67.75) * mm, "end": v(39.2, 68.2) * mm});
            skArc(sketch, "E258", {"start": v(43.55, 65.64) * mm, "mid": v(41.23, 66.48) * mm, "end": v(38.91, 67.32) * mm});
            skSolve(sketch);
        }
        {
            var Q0;
            Q0=qCreatedBy(makeId("Front.planeOp"),FACE);
            var sketch = newSketch(context, id + "F5", { "sketchPlane" : qUnion([Q0])});
            skArc(sketch, "E259", {"start": v(-8.36, 21.5) * mm, "mid": v(-8.52, 20.16) * mm, "end": v(-8.38, 18.81) * mm});
            skArc(sketch, "E260", {"start": v(-8.38, 18.81) * mm, "mid": v(-4.88, 18.72) * mm, "end": v(-1.39, 18.81) * mm});
            skArc(sketch, "E261", {"start": v(-8.36, 21.5) * mm, "mid": v(-4.86, 21.63) * mm, "end": v(-1.37, 21.75) * mm});
            skArc(sketch, "E262", {"start": v(8.93, 19.5) * mm, "mid": v(9.08, 20.98) * mm, "end": v(8.91, 22.45) * mm});
            skArc(sketch, "E263", {"start": v(2.71, 18.81) * mm, "mid": v(5.82, 19.16) * mm, "end": v(8.93, 19.5) * mm});
            skArc(sketch, "E264", {"start": v(2.7, 21.77) * mm, "mid": v(5.81, 22.04) * mm, "end": v(8.91, 22.45) * mm});
            skLineSegment(sketch, "E265", {"start": v(-1.37, 21.75) * mm, "end": v(-1.37, 22.1) * mm});
            skLineSegment(sketch, "E266", {"start": v(-1.37, 22.1) * mm, "end": v(2.71, 22.1) * mm});
            skLineSegment(sketch, "E267", {"start": v(2.71, 22.1) * mm, "end": v(2.7, 21.77) * mm});
            skLineSegment(sketch, "E268", {"start": v(2.71, 18.81) * mm, "end": v(2.71, 18.28) * mm});
            skLineSegment(sketch, "E269", {"start": v(2.71, 18.28) * mm, "end": v(-1.37, 18.28) * mm});
            skLineSegment(sketch, "E270", {"start": v(-1.37, 18.28) * mm, "end": v(-1.39, 18.81) * mm});
            skLineSegment(sketch, "E271", {"start": v(-0.75, 18.81) * mm, "end": v(-0.75, 21.54) * mm});
            skLineSegment(sketch, "E272", {"start": v(-0.75, 21.54) * mm, "end": v(2.1, 21.54) * mm});
            skLineSegment(sketch, "E273", {"start": v(2.1, 21.54) * mm, "end": v(2.1, 18.81) * mm});
            skLineSegment(sketch, "E274", {"start": v(2.1, 18.81) * mm, "end": v(-0.75, 18.81) * mm});
            skSolve(sketch);
        }
        {
            var Q0;
            Q0=qCreatedBy(makeId("Front.planeOp"),FACE);
            var sketch = newSketch(context, id + "F6", { "sketchPlane" : qUnion([Q0])});
            skArc(sketch, "E275", {"start": v(-36.69, 61.98) * mm, "mid": v(-31.28, 53.44) * mm, "end": v(-22.75, 48.04) * mm});
            skArc(sketch, "E276", {"start": v(0.44, 36.16) * mm, "mid": v(-11.08, 42.24) * mm, "end": v(-22.75, 48.04) * mm});
            skArc(sketch, "E277", {"start": v(23.74, 48.04) * mm, "mid": v(12.1, 42.09) * mm, "end": v(0.44, 36.16) * mm});
            skArc(sketch, "E278", {"start": v(23.74, 48.04) * mm, "mid": v(26.22, 49.58) * mm, "end": v(28.62, 51.25) * mm});
            skArc(sketch, "E279", {"start": v(24.67, 54.32) * mm, "mid": v(31.13, 58.2) * mm, "end": v(36.04, 63.91) * mm});
            skArc(sketch, "E280", {"start": v(12.25, 48.7) * mm, "mid": v(18.6, 51.2) * mm, "end": v(24.67, 54.32) * mm});
            skArc(sketch, "E281", {"start": v(1.1, 42.74) * mm, "mid": v(6.68, 45.7) * mm, "end": v(12.25, 48.7) * mm});
            skArc(sketch, "E282", {"start": v(-16, 50.1) * mm, "mid": v(-13.7, 49.33) * mm, "end": v(-11.37, 48.7) * mm});
            skArc(sketch, "E283", {"start": v(-11.37, 48.7) * mm, "mid": v(-5.75, 45.6) * mm, "end": v(0, 42.74) * mm});
            skArc(sketch, "E284", {"start": v(-11.53, 42.46) * mm, "mid": v(-13.47, 41.1) * mm, "end": v(-15.2, 39.47) * mm});
            skArc(sketch, "E285", {"start": v(-38.14, 60.8) * mm, "mid": v(-38.45, 60.39) * mm, "end": v(-38.65, 59.92) * mm});
            skArc(sketch, "E286", {"start": v(-4.87, 50.57) * mm, "mid": v(-2.8, 48.82) * mm, "end": v(-0.18, 48.07) * mm});
            skArc(sketch, "E287", {"start": v(-0.67, 48.12) * mm, "mid": v(-6.1, 45.3) * mm, "end": v(-11.53, 42.46) * mm});
            skArc(sketch, "E288", {"start": v(-4.87, 50.57) * mm, "mid": v(-6.16, 50.27) * mm, "end": v(-7.45, 49.93) * mm});
            skArc(sketch, "E289", {"start": v(-16, 50.1) * mm, "mid": v(-11.72, 49.86) * mm, "end": v(-7.45, 49.93) * mm});
            skArc(sketch, "E290", {"start": v(-16, 50.1) * mm, "mid": v(-18.88, 50.49) * mm, "end": v(-21.77, 50.88) * mm});
            skArc(sketch, "E291", {"start": v(-21.77, 50.88) * mm, "mid": v(-23.21, 52.47) * mm, "end": v(-24.75, 53.97) * mm});
            skLineSegment(sketch, "E292", {"start": v(-36, 62.53) * mm, "end": v(-38.14, 60.8) * mm});
            skArc(sketch, "E293", {"start": v(-38.65, 59.92) * mm, "mid": v(-35.55, 55.57) * mm, "end": v(-32.1, 51.5) * mm});
            skArc(sketch, "E294", {"start": v(-32.1, 51.5) * mm, "mid": v(-29.54, 48.64) * mm, "end": v(-26.75, 46.03) * mm});
            skArc(sketch, "E295", {"start": v(-26.75, 46.03) * mm, "mid": v(-24.28, 44.4) * mm, "end": v(-21.69, 42.97) * mm});
            skArc(sketch, "E296", {"start": v(-15.2, 39.47) * mm, "mid": v(-18.43, 41.25) * mm, "end": v(-21.69, 42.97) * mm});
            skArc(sketch, "E297", {"start": v(-12.5, 37.25) * mm, "mid": v(-13.7, 38.53) * mm, "end": v(-15.2, 39.47) * mm});
            skArc(sketch, "E298", {"start": v(-12.5, 37.25) * mm, "mid": v(-12.12, 33.54) * mm, "end": v(-10.7, 30.1) * mm});
            skArc(sketch, "E299", {"start": v(-8.8, 24.88) * mm, "mid": v(-9.53, 27.57) * mm, "end": v(-10.7, 30.1) * mm});
            skLineSegment(sketch, "E300", {"start": v(0.44, 41.38) * mm, "end": v(0.5, 22.1) * mm});
            skLineSegment(sketch, "E301", {"start": v(0.5, 18.28) * mm, "end": v(0.5, 5.88) * mm});
            skLineSegment(sketch, "E302", {"start": v(0.9, 48.07) * mm, "end": v(1.1, 42.74) * mm});
            skLineSegment(sketch, "E303", {"start": v(-0.18, 48.07) * mm, "end": v(0, 42.74) * mm});
            skArc(sketch, "E304", {"start": v(0.9, 48.07) * mm, "mid": v(3.1, 48.92) * mm, "end": v(4.82, 50.54) * mm});
            skArc(sketch, "E305", {"start": v(14.54, 41) * mm, "mid": v(13.56, 41.69) * mm, "end": v(12.53, 42.3) * mm});
            skArc(sketch, "E306", {"start": v(1.54, 48.22) * mm, "mid": v(7, 45.2) * mm, "end": v(12.53, 42.3) * mm});
            skArc(sketch, "E307", {"start": v(-8.36, 21.52) * mm, "mid": v(-8.4, 23.22) * mm, "end": v(-8.8, 24.88) * mm});
            skArc(sketch, "E308", {"start": v(-8.36, 18.8) * mm, "mid": v(-11.24, 11.56) * mm, "end": v(-13.09, 4) * mm});
            skArc(sketch, "E309", {"start": v(-13.09, 4) * mm, "mid": v(-14.1, -3.89) * mm, "end": v(-14.47, -11.83) * mm});
            skArc(sketch, "E310", {"start": v(-14.47, -11.83) * mm, "mid": v(-15.15, -15.38) * mm, "end": v(-13.2, -18.43) * mm});
            skArc(sketch, "E311", {"start": v(-10.37, -21.76) * mm, "mid": v(-11.72, -20.04) * mm, "end": v(-13.2, -18.43) * mm});
            skArc(sketch, "E312", {"start": v(-6.08, -27.2) * mm, "mid": v(-8.2, -24.46) * mm, "end": v(-10.37, -21.76) * mm});
            skArc(sketch, "E313", {"start": v(1.5, -37.97) * mm, "mid": v(-1.79, -32.23) * mm, "end": v(-6.08, -27.2) * mm});
            skLineSegment(sketch, "E314", {"start": v(1.5, -37.97) * mm, "end": v(5.94, -36.04) * mm});
            skArc(sketch, "E315", {"start": v(2.09, -26.95) * mm, "mid": v(3.78, -31.6) * mm, "end": v(5.94, -36.04) * mm});
            skArc(sketch, "E316", {"start": v(2.09, -26.95) * mm, "mid": v(0.86, -23.47) * mm, "end": v(-0.63, -20.1) * mm});
            skArc(sketch, "E317", {"start": v(-0.63, -20.1) * mm, "mid": v(-2.05, -17.89) * mm, "end": v(-4.04, -16.17) * mm});
            skArc(sketch, "E318", {"start": v(-5.01, -10.64) * mm, "mid": v(-5.47, -13.57) * mm, "end": v(-4.04, -16.17) * mm});
            skArc(sketch, "E319", {"start": v(-5.01, -10.64) * mm, "mid": v(-2.75, -6.82) * mm, "end": v(-1.16, -2.67) * mm});
            skArc(sketch, "E320", {"start": v(-1.16, -2.67) * mm, "mid": v(0.16, 1.5) * mm, "end": v(0.5, 5.88) * mm});
            skArc(sketch, "E321", {"start": v(3.65, -2.67) * mm, "mid": v(2.12, 1.62) * mm, "end": v(0.5, 5.88) * mm});
            skArc(sketch, "E322", {"start": v(3.65, -2.67) * mm, "mid": v(5.78, -7.2) * mm, "end": v(8.47, -11.4) * mm});
            skArc(sketch, "E323", {"start": v(8.47, -11.4) * mm, "mid": v(8.5, -12.63) * mm, "end": v(8.66, -13.84) * mm});
            skArc(sketch, "E324", {"start": v(2.86, -17.1) * mm, "mid": v(5.77, -15.5) * mm, "end": v(8.66, -13.84) * mm});
            skArc(sketch, "E325", {"start": v(2.86, -17.1) * mm, "mid": v(0.89, -18.28) * mm, "end": v(-0.71, -19.91) * mm});
            skArc(sketch, "E326", {"start": v(-10.5, -32.5) * mm, "mid": v(-8.2, -29.9) * mm, "end": v(-6.08, -27.2) * mm});
            skArc(sketch, "E327", {"start": v(-10.5, -32.5) * mm, "mid": v(-8.45, -34.68) * mm, "end": v(-5.65, -35.76) * mm});
            skArc(sketch, "E328", {"start": v(-2.86, -30.79) * mm, "mid": v(-4.52, -33.12) * mm, "end": v(-5.65, -35.76) * mm});
            skArc(sketch, "E329", {"start": v(2.09, -26.95) * mm, "mid": v(10.33, -22.33) * mm, "end": v(17.5, -16.17) * mm});
            skArc(sketch, "E330", {"start": v(17.5, -16.17) * mm, "mid": v(17.1, -7.98) * mm, "end": v(15.83, 0.13) * mm});
            skArc(sketch, "E331", {"start": v(15.83, 0.13) * mm, "mid": v(14.53, 5.32) * mm, "end": v(13.21, 10.51) * mm});
            skArc(sketch, "E332", {"start": v(13.21, 10.51) * mm, "mid": v(11.6, 15.26) * mm, "end": v(8.93, 19.51) * mm});
            skLineSegment(sketch, "E333", {"start": v(8.93, 19.51) * mm, "end": v(2.7, 18.81) * mm});
            skLineSegment(sketch, "E334", {"start": v(2.7, 18.81) * mm, "end": v(2.7, 18.28) * mm});
            skLineSegment(sketch, "E335", {"start": v(2.7, 18.28) * mm, "end": v(-1.38, 18.28) * mm});
            skLineSegment(sketch, "E336", {"start": v(-1.38, 18.28) * mm, "end": v(-1.38, 18.81) * mm});
            skLineSegment(sketch, "E337", {"start": v(-1.38, 18.81) * mm, "end": v(-8.36, 18.8) * mm});
            skLineSegment(sketch, "E338", {"start": v(-8.36, 21.52) * mm, "end": v(-1.37, 21.76) * mm});
            skLineSegment(sketch, "E339", {"start": v(-1.37, 21.76) * mm, "end": v(-1.37, 22.1) * mm});
            skLineSegment(sketch, "E340", {"start": v(-1.37, 22.1) * mm, "end": v(0.5, 22.1) * mm});
            skLineSegment(sketch, "E341", {"start": v(0.5, 22.1) * mm, "end": v(2.7, 22.1) * mm});
            skLineSegment(sketch, "E342", {"start": v(2.7, 22.1) * mm, "end": v(2.7, 21.76) * mm});
            skLineSegment(sketch, "E343", {"start": v(2.7, 21.76) * mm, "end": v(8.92, 22.46) * mm});
            skArc(sketch, "E344", {"start": v(9.44, 25.23) * mm, "mid": v(9.05, 23.86) * mm, "end": v(8.92, 22.46) * mm});
            skArc(sketch, "E345", {"start": v(9.44, 25.23) * mm, "mid": v(10.74, 29.53) * mm, "end": v(12.02, 33.84) * mm});
            skArc(sketch, "E346", {"start": v(14.54, 41) * mm, "mid": v(12.75, 37.6) * mm, "end": v(12.02, 33.84) * mm});
            skArc(sketch, "E347", {"start": v(18.04, 43.23) * mm, "mid": v(16.09, 42.44) * mm, "end": v(14.54, 41) * mm});
            skArc(sketch, "E348", {"start": v(18.04, 43.23) * mm, "mid": v(21.55, 44.53) * mm, "end": v(24.7, 46.53) * mm});
            skArc(sketch, "E349", {"start": v(24.7, 46.53) * mm, "mid": v(26.87, 48.72) * mm, "end": v(28.62, 51.25) * mm});
            skArc(sketch, "E350", {"start": v(28.62, 51.25) * mm, "mid": v(32.01, 55.7) * mm, "end": v(34.57, 60.7) * mm});
            skArc(sketch, "E351", {"start": v(34.57, 60.7) * mm, "mid": v(35.47, 62.23) * mm, "end": v(36.04, 63.91) * mm});
            skLineSegment(sketch, "E352", {"start": v(36.04, 63.91) * mm, "end": v(32.24, 65.2) * mm});
            skArc(sketch, "E353", {"start": v(32.18, 64.66) * mm, "mid": v(32.24, 64.92) * mm, "end": v(32.24, 65.2) * mm});
            skArc(sketch, "E354", {"start": v(25.94, 58.47) * mm, "mid": v(29.17, 61.45) * mm, "end": v(32.18, 64.66) * mm});
            skArc(sketch, "E355", {"start": v(21.24, 53.44) * mm, "mid": v(23.6, 55.95) * mm, "end": v(25.94, 58.47) * mm});
            skArc(sketch, "E356", {"start": v(14.9, 51.11) * mm, "mid": v(18.2, 51.95) * mm, "end": v(21.24, 53.44) * mm});
            skArc(sketch, "E357", {"start": v(7.97, 50.06) * mm, "mid": v(11.46, 50.42) * mm, "end": v(14.9, 51.11) * mm});
            skArc(sketch, "E358", {"start": v(4.82, 50.54) * mm, "mid": v(6.39, 50.28) * mm, "end": v(7.97, 50.06) * mm});
            skArc(sketch, "E359", {"start": v(-33.88, 60.84) * mm, "mid": v(-35.66, 59.14) * mm, "end": v(-36.51, 56.84) * mm});
            skArc(sketch, "E360", {"start": v(-29.38, 57.38) * mm, "mid": v(-31.98, 55.7) * mm, "end": v(-33.4, 52.96) * mm});
            skArc(sketch, "E361", {"start": v(-24.75, 53.97) * mm, "mid": v(-27.53, 51.6) * mm, "end": v(-29.32, 48.42) * mm});
            skArc(sketch, "E362", {"start": v(-19.47, 50.57) * mm, "mid": v(-22.66, 48.04) * mm, "end": v(-23.92, 44.18) * mm});
            skArc(sketch, "E363", {"start": v(-11.37, 48.7) * mm, "mid": v(-16.13, 45.98) * mm, "end": v(-19.99, 42.08) * mm});
            skArc(sketch, "E364", {"start": v(-9.2, 49.87) * mm, "mid": v(-10.3, 49.31) * mm, "end": v(-11.37, 48.7) * mm});
            skArc(sketch, "E365", {"start": v(19.4, 43.64) * mm, "mid": v(16.23, 46.73) * mm, "end": v(12.25, 48.7) * mm});
            skArc(sketch, "E366", {"start": v(12.25, 48.7) * mm, "mid": v(10.86, 49.46) * mm, "end": v(9.45, 50.17) * mm});
            skArc(sketch, "E367", {"start": v(24.7, 46.53) * mm, "mid": v(22.12, 49.78) * mm, "end": v(18.71, 52.15) * mm});
            skArc(sketch, "E368", {"start": v(28.62, 51.25) * mm, "mid": v(25.93, 53.5) * mm, "end": v(22.86, 55.16) * mm});
            skArc(sketch, "E369", {"start": v(32.26, 56.11) * mm, "mid": v(29.28, 57.77) * mm, "end": v(25.94, 58.47) * mm});
            skArc(sketch, "E370", {"start": v(34.57, 60.7) * mm, "mid": v(32.62, 62.06) * mm, "end": v(30.3, 62.6) * mm});
            skArc(sketch, "E371", {"start": v(0, 41.95) * mm, "mid": v(0.1, 41.57) * mm, "end": v(0.44, 41.38) * mm});
            skArc(sketch, "E372", {"start": v(0.44, 41.38) * mm, "mid": v(0.9, 41.51) * mm, "end": v(1.1, 41.95) * mm});
            skLineSegment(sketch, "E373", {"start": v(1.1, 41.95) * mm, "end": v(1.1, 42.74) * mm});
            skLineSegment(sketch, "E374", {"start": v(0, 41.95) * mm, "end": v(0, 42.74) * mm});
            skArc(sketch, "E375", {"start": v(1.1, 42.07) * mm, "mid": v(6.72, 39.14) * mm, "end": v(12.35, 36.24) * mm});
            skArc(sketch, "E376", {"start": v(0, 42.07) * mm, "mid": v(-6.27, 38.92) * mm, "end": v(-12.46, 35.6) * mm});
            skArc(sketch, "E377", {"start": v(0.47, 29.77) * mm, "mid": v(-6, 33.27) * mm, "end": v(-12.5, 36.67) * mm});
            skArc(sketch, "E378", {"start": v(0.44, 36.16) * mm, "mid": v(-5.14, 33.13) * mm, "end": v(-10.7, 30.1) * mm});
            skArc(sketch, "E379", {"start": v(11.05, 30.59) * mm, "mid": v(5.76, 33.4) * mm, "end": v(0.44, 36.16) * mm});
            skArc(sketch, "E380", {"start": v(0.47, 29.77) * mm, "mid": v(6.46, 32.91) * mm, "end": v(12.35, 36.24) * mm});
            skArc(sketch, "E381", {"start": v(0.47, 29.77) * mm, "mid": v(4.95, 27.5) * mm, "end": v(9.44, 25.23) * mm});
            skArc(sketch, "E382", {"start": v(0.49, 23.58) * mm, "mid": v(5.52, 26.2) * mm, "end": v(10.53, 28.84) * mm});
            skArc(sketch, "E383", {"start": v(-10.2, 29.15) * mm, "mid": v(-4.88, 26.33) * mm, "end": v(0.49, 23.58) * mm});
            skArc(sketch, "E384", {"start": v(0.47, 29.77) * mm, "mid": v(-4.21, 27.42) * mm, "end": v(-8.8, 24.88) * mm});
            skArc(sketch, "E385", {"start": v(3.5, 21.84) * mm, "mid": v(2.02, 22.75) * mm, "end": v(0.49, 23.58) * mm});
            skArc(sketch, "E386", {"start": v(-2.95, 21.7) * mm, "mid": v(-1.22, 22.62) * mm, "end": v(0.49, 23.58) * mm});
            skArc(sketch, "E387", {"start": v(-7.8, 21.54) * mm, "mid": v(-8.05, 21.77) * mm, "end": v(-8.33, 21.97) * mm});
            skArc(sketch, "E388", {"start": v(8.37, 22.4) * mm, "mid": v(8.66, 22.63) * mm, "end": v(8.93, 22.9) * mm});
            skArc(sketch, "E389", {"start": v(8.31, 19.44) * mm, "mid": v(8.85, 19.1) * mm, "end": v(9.44, 18.85) * mm});
            skArc(sketch, "E390", {"start": v(-7.78, 18.8) * mm, "mid": v(-8.14, 18.66) * mm, "end": v(-8.5, 18.5) * mm});
            skArc(sketch, "E391", {"start": v(0.5, 17.26) * mm, "mid": v(-0.94, 18.06) * mm, "end": v(-2.4, 18.8) * mm});
            skArc(sketch, "E392", {"start": v(0.5, 17.26) * mm, "mid": v(2.12, 18) * mm, "end": v(3.65, 18.92) * mm});
            skArc(sketch, "E393", {"start": v(-11.44, 10.92) * mm, "mid": v(-5.47, 14.08) * mm, "end": v(0.5, 17.26) * mm});
            skArc(sketch, "E394", {"start": v(13.21, 10.51) * mm, "mid": v(6.9, 13.96) * mm, "end": v(0.5, 17.26) * mm});
            skArc(sketch, "E395", {"start": v(0.5, 10.99) * mm, "mid": v(7.73, 7.08) * mm, "end": v(15.03, 3.3) * mm});
            skArc(sketch, "E396", {"start": v(-13.12, 3.8) * mm, "mid": v(-6.3, 7.38) * mm, "end": v(0.5, 10.99) * mm});
            skArc(sketch, "E397", {"start": v(0.5, 10.99) * mm, "mid": v(-4.5, 13.64) * mm, "end": v(-9.5, 16.24) * mm});
            skArc(sketch, "E398", {"start": v(11.01, 16.4) * mm, "mid": v(5.74, 13.72) * mm, "end": v(0.5, 10.99) * mm});
            skArc(sketch, "E399", {"start": v(0.5, 4.63) * mm, "mid": v(-5.43, 7.85) * mm, "end": v(-11.44, 10.92) * mm});
            skArc(sketch, "E400", {"start": v(0.92, 4.78) * mm, "mid": v(6.99, 8) * mm, "end": v(13.05, 11.23) * mm});
            skArc(sketch, "E401", {"start": v(1.1, 4.34) * mm, "mid": v(8.8, 0.19) * mm, "end": v(16.56, -3.85) * mm});
            skArc(sketch, "E402", {"start": v(14.45, 5.62) * mm, "mid": v(8.62, 2.68) * mm, "end": v(2.84, -0.37) * mm});
            skArc(sketch, "E403", {"start": v(15.83, 0.13) * mm, "mid": v(10.37, -2.7) * mm, "end": v(4.96, -5.62) * mm});
            skArc(sketch, "E404", {"start": v(4, -3.5) * mm, "mid": v(10.63, -7.13) * mm, "end": v(17.33, -10.64) * mm});
            skArc(sketch, "E405", {"start": v(16.84, -5.76) * mm, "mid": v(12.29, -8.02) * mm, "end": v(8.01, -10.78) * mm});
            skArc(sketch, "E406", {"start": v(8.47, -12.07) * mm, "mid": v(10.4, -13.42) * mm, "end": v(12.41, -14.63) * mm});
            skArc(sketch, "E407", {"start": v(12.41, -14.63) * mm, "mid": v(15.03, -13.75) * mm, "end": v(17.42, -12.38) * mm});
            skArc(sketch, "E408", {"start": v(12.41, -14.63) * mm, "mid": v(13.17, -17.05) * mm, "end": v(14.09, -19.42) * mm});
            skArc(sketch, "E409", {"start": v(7.64, -14.43) * mm, "mid": v(10.02, -14.62) * mm, "end": v(12.41, -14.63) * mm});
            skArc(sketch, "E410", {"start": v(9.61, -22.82) * mm, "mid": v(8.14, -18.92) * mm, "end": v(6.41, -15.13) * mm});
            skArc(sketch, "E411", {"start": v(1.77, -17.67) * mm, "mid": v(7.5, -19.36) * mm, "end": v(13.42, -19.98) * mm});
            skArc(sketch, "E412", {"start": v(4.48, -24.37) * mm, "mid": v(3.17, -21) * mm, "end": v(1.77, -17.67) * mm});
            skArc(sketch, "E413", {"start": v(4.48, -24.37) * mm, "mid": v(4.7, -24.98) * mm, "end": v(5, -25.55) * mm});
            skArc(sketch, "E414", {"start": v(0.95, -23.7) * mm, "mid": v(3.75, -24.26) * mm, "end": v(6.58, -24.7) * mm});
            skArc(sketch, "E415", {"start": v(-5.71, -27.55) * mm, "mid": v(-5.3, -30.19) * mm, "end": v(-4.23, -32.64) * mm});
            skArc(sketch, "E416", {"start": v(-4.23, -32.64) * mm, "mid": v(-6.75, -31.87) * mm, "end": v(-9.28, -31.17) * mm});
            skArc(sketch, "E417", {"start": v(0.55, -36.04) * mm, "mid": v(3.25, -36.08) * mm, "end": v(5.94, -36.04) * mm});
            skArc(sketch, "E418", {"start": v(0.55, -36.04) * mm, "mid": v(2.68, -34.26) * mm, "end": v(3.85, -31.75) * mm});
            skArc(sketch, "E419", {"start": v(-2.39, -31.4) * mm, "mid": v(0.62, -31.5) * mm, "end": v(3.62, -31.21) * mm});
            skArc(sketch, "E420", {"start": v(-2.39, -31.4) * mm, "mid": v(-0.14, -28.97) * mm, "end": v(1.9, -26.38) * mm});
            skArc(sketch, "E421", {"start": v(-7.52, -25.33) * mm, "mid": v(-2.82, -25.98) * mm, "end": v(1.9, -26.38) * mm});
            skArc(sketch, "E422", {"start": v(-6.08, -27.2) * mm, "mid": v(-3.19, -23.9) * mm, "end": v(-0.44, -20.48) * mm});
            skArc(sketch, "E423", {"start": v(-12.67, -18.98) * mm, "mid": v(-6.68, -19.92) * mm, "end": v(-0.63, -20.1) * mm});
            skArc(sketch, "E424", {"start": v(-4.04, -16.17) * mm, "mid": v(-6.76, -19.54) * mm, "end": v(-9.4, -22.95) * mm});
            skArc(sketch, "E425", {"start": v(-13.2, -18.43) * mm, "mid": v(-11.31, -16.4) * mm, "end": v(-9.7, -14.13) * mm});
            skArc(sketch, "E426", {"start": v(-9.7, -14.13) * mm, "mid": v(-7.3, -14.72) * mm, "end": v(-4.87, -15.17) * mm});
            skArc(sketch, "E427", {"start": v(-5.01, -10.64) * mm, "mid": v(-7.4, -12.34) * mm, "end": v(-9.7, -14.13) * mm});
            skArc(sketch, "E428", {"start": v(-14.72, -12.26) * mm, "mid": v(-12.22, -13.22) * mm, "end": v(-9.7, -14.13) * mm});
            skArc(sketch, "E429", {"start": v(-11.43, -7.94) * mm, "mid": v(-12.98, -9.39) * mm, "end": v(-14.46, -10.92) * mm});
            skArc(sketch, "E430", {"start": v(-11.43, -7.94) * mm, "mid": v(-8.17, -9.36) * mm, "end": v(-4.74, -10.25) * mm});
            skArc(sketch, "E431", {"start": v(-11.43, -7.94) * mm, "mid": v(-12.85, -7.2) * mm, "end": v(-14.29, -6.5) * mm});
            skArc(sketch, "E432", {"start": v(-1.16, -2.67) * mm, "mid": v(-6.31, -5.27) * mm, "end": v(-11.43, -7.94) * mm});
            skArc(sketch, "E433", {"start": v(-2.54, -6.37) * mm, "mid": v(-8.07, -3.33) * mm, "end": v(-13.74, -0.55) * mm});
            skArc(sketch, "E434", {"start": v(-14, -2.95) * mm, "mid": v(-6.72, 0.79) * mm, "end": v(0.5, 4.63) * mm});
            skArc(sketch, "E435", {"start": v(-0.53, -1.09) * mm, "mid": v(-6.67, 2.18) * mm, "end": v(-12.82, 5.4) * mm});
            skArc(sketch, "E436", {"start": v(-36, 62.53) * mm, "mid": v(-30.48, 58.1) * mm, "end": v(-24.75, 53.97) * mm});
            skSolve(sketch);
        }
        {
            var Q0;
            Q0=qCreatedBy(makeId("Front.planeOp"),FACE);
            var sketch = newSketch(context, id + "F7", { "sketchPlane" : qUnion([Q0])});
            skArc(sketch, "E437", {"start": v(-4.87, 50.59) * mm, "mid": v(-4.38, 50.92) * mm, "end": v(-3.93, 51.3) * mm});
            skArc(sketch, "E438", {"start": v(-3.93, 51.3) * mm, "mid": v(-2.8, 50.21) * mm, "end": v(-1.4, 49.56) * mm});
            skArc(sketch, "E439", {"start": v(-1.4, 49.56) * mm, "mid": v(0.04, 49.35) * mm, "end": v(1.45, 49.64) * mm});
            skArc(sketch, "E440", {"start": v(1.45, 49.64) * mm, "mid": v(2.8, 50.25) * mm, "end": v(4.05, 51.06) * mm});
            skArc(sketch, "E441", {"start": v(4.05, 51.06) * mm, "mid": v(4.37, 50.71) * mm, "end": v(4.81, 50.55) * mm});
            skArc(sketch, "E442", {"start": v(0.9, 48.08) * mm, "mid": v(3.1, 48.93) * mm, "end": v(4.81, 50.55) * mm});
            skArc(sketch, "E443", {"start": v(-4.87, 50.59) * mm, "mid": v(-2.8, 48.82) * mm, "end": v(-0.19, 48.07) * mm});
            skArc(sketch, "E444", {"start": v(0, 41.96) * mm, "mid": v(0.1, 41.58) * mm, "end": v(0.44, 41.38) * mm});
            skArc(sketch, "E445", {"start": v(0.44, 41.38) * mm, "mid": v(0.9, 41.51) * mm, "end": v(1.09, 41.95) * mm});
            skLineSegment(sketch, "E446", {"start": v(0, 41.96) * mm, "end": v(-0.19, 48.07) * mm});
            skLineSegment(sketch, "E447", {"start": v(0.9, 48.08) * mm, "end": v(1.09, 41.95) * mm});
            skSolve(sketch);
        }
        {
            var Q0;
            Q0 = qSketchRegion(id + "F0", true);
            extrude(context, id + "F8", {"entities" : qUnion([Q0]), "depth" : 6.5 * mm, "offsetDistance" : 25 * mm});
        }
        {
            var Q0;
            Q0 = qSketchRegion(id + "F1", true);
            extrude(context, id + "F9", {"entities" : qUnion([Q0]), "depth" : 7 * mm, "offsetDistance" : 25 * mm});
        }
        {
            var Q0;
            Q0 = qSketchRegion(id + "F3", true);
            extrude(context, id + "F10", {"entities" : qUnion([Q0]), "operationType" : NewBodyOperationType.ADD, "depth" : 5.75 * mm, "offsetDistance" : 25 * mm});
        }
        {
            var Q0;
            Q0 = qSketchRegion(id + "F4", true);
            extrude(context, id + "F11", {"entities" : qUnion([Q0]), "depth" : 5.5 * mm, "offsetDistance" : 25 * mm});
        }
        {
            var Q0;
            Q0 = qSketchRegion(id + "F7", true);
            extrude(context, id + "F12", {"entities" : qUnion([Q0]), "depth" : 7 * mm, "offsetDistance" : 25 * mm});
        }
        {
            var Q0;
            Q0 = qSketchRegion(id + "F5", true);
            extrude(context, id + "F13", {"entities" : qUnion([Q0]), "depth" : 7.5 * mm, "offsetDistance" : 25 * mm});
        }
        {
            var Q0;
            {var subQ0=sQuery(id+"F6.wireOp",EDGE,"E376");var subQ1=sQuery(id+"F6.wireOp",EDGE,"E298");var subQ2=makeQuery(id+"F6.imprint","INTERSECT",VERTEX,{"derivedFrom":[subQ1,subQ0]});Q0=makeQuery(id+"F6.imprint","IMPRINT",FACE,{"disambiguationData":[TD([[makeQuery(id+"F6.imprint","IMPRINT",EDGE,{"disambiguationData":[TD([[subQ2,1.0]])],"derivedFrom":subQ1}),1.0]])]});}
            var Q1;
            {var subQ1=sQuery(id+"F6.wireOp",EDGE,"E276");var subQ3=sQuery(id+"F6.wireOp",EDGE,"E376");var subQ4=makeQuery(id+"F6.imprint","INTERSECT",VERTEX,{"derivedFrom":[subQ1,subQ3]});Q1=makeQuery(id+"F6.imprint","IMPRINT",FACE,{"disambiguationData":[TD([[makeQuery(id+"F6.imprint","IMPRINT",EDGE,{"disambiguationData":[TD([[subQ4,-1.0]])],"derivedFrom":subQ3}),1.0]])]});}
            var Q2;
            {var subQ0=sQuery(id+"F6.wireOp",EDGE,"E292");var subQ1=sQuery(id+"F6.wireOp",EDGE,"E275");var subQ2=makeQuery(id+"F6.imprint","INTERSECT",VERTEX,{"derivedFrom":[subQ1,subQ0]});Q2=makeQuery(id+"F6.imprint","IMPRINT",FACE,{"disambiguationData":[TD([[makeQuery(id+"F6.imprint","IMPRINT",EDGE,{"disambiguationData":[TD([[subQ2,-1.0]])],"derivedFrom":subQ1}),1.0]])]});}
            var Q3;
            {var subQ0=sQuery(id+"F6.wireOp",EDGE,"E359");var subQ1=sQuery(id+"F6.wireOp",EDGE,"E275");var subQ2=makeQuery(id+"F6.imprint","INTERSECT",VERTEX,{"derivedFrom":[subQ1,subQ0]});Q3=makeQuery(id+"F6.imprint","IMPRINT",FACE,{"disambiguationData":[TD([[makeQuery(id+"F6.imprint","IMPRINT",EDGE,{"disambiguationData":[TD([[subQ2,-1.0]])],"derivedFrom":subQ1}),-1.0]])]});}
            var Q4;
            {var subQ0=sQuery(id+"F6.wireOp",EDGE,"E360");var subQ1=sQuery(id+"F6.wireOp",EDGE,"E275");var subQ2=makeQuery(id+"F6.imprint","INTERSECT",VERTEX,{"derivedFrom":[subQ1,subQ0]});Q4=makeQuery(id+"F6.imprint","IMPRINT",FACE,{"disambiguationData":[TD([[makeQuery(id+"F6.imprint","IMPRINT",EDGE,{"disambiguationData":[TD([[subQ2,-1.0]])],"derivedFrom":subQ1}),1.0]])]});}
            var Q5;
            {var subQ5=sQuery(id+"F6.wireOp",EDGE,"E276");var subQ6=sQuery(id+"F6.wireOp",EDGE,"E275");var subQ7=makeQuery(id+"F6.imprint","INTERSECT",VERTEX,{"derivedFrom":[subQ6,subQ5]});Q5=makeQuery(id+"F6.imprint","IMPRINT",FACE,{"disambiguationData":[TD([[makeQuery(id+"F6.imprint","IMPRINT",EDGE,{"disambiguationData":[TD([[subQ7,1.0]])],"derivedFrom":subQ6}),-1.0]])]});}
            var Q6;
            {var subQ1=sQuery(id+"F6.wireOp",EDGE,"E282");Q6=makeQuery(id+"F6.imprint","IMPRINT",FACE,{"disambiguationData":[TD([[makeQuery(id+"F6.imprint","IMPRINT",EDGE,{"derivedFrom":subQ1}),-1.0]])]});}
            var Q7;
            {var subQ0=sQuery(id+"F6.wireOp",EDGE,"E284");Q7=makeQuery(id+"F6.imprint","IMPRINT",FACE,{"disambiguationData":[TD([[makeQuery(id+"F6.imprint","IMPRINT",EDGE,{"derivedFrom":subQ0}),-1.0]])]});}
            var Q8;
            {var subQ0=sQuery(id+"F6.wireOp",EDGE,"E374");var subQ3=sQuery(id+"F6.wireOp",EDGE,"E376");var subQ4=makeQuery(id+"F6.imprint","INTERSECT",VERTEX,{"derivedFrom":[subQ0,subQ3]});Q8=makeQuery(id+"F6.imprint","IMPRINT",FACE,{"disambiguationData":[TD([[makeQuery(id+"F6.imprint","IMPRINT",EDGE,{"disambiguationData":[TD([[subQ4,-1.0]])],"derivedFrom":subQ3}),-1.0]])]});}
            var Q9;
            {var subQ0=sQuery(id+"F6.wireOp",EDGE,"E288");Q9=makeQuery(id+"F6.imprint","IMPRINT",FACE,{"disambiguationData":[TD([[makeQuery(id+"F6.imprint","IMPRINT",EDGE,{"derivedFrom":subQ0}),1.0]])]});}
            var Q10;
            {var subQ0=sQuery(id+"F6.wireOp",EDGE,"E358");Q10=makeQuery(id+"F6.imprint","IMPRINT",FACE,{"disambiguationData":[TD([[makeQuery(id+"F6.imprint","IMPRINT",EDGE,{"derivedFrom":subQ0}),-1.0]])]});}
            var Q11;
            {var subQ0=sQuery(id+"F6.wireOp",EDGE,"E373");var subQ3=sQuery(id+"F6.wireOp",EDGE,"E375");var subQ4=makeQuery(id+"F6.imprint","INTERSECT",VERTEX,{"derivedFrom":[subQ0,subQ3]});Q11=makeQuery(id+"F6.imprint","IMPRINT",FACE,{"disambiguationData":[TD([[makeQuery(id+"F6.imprint","IMPRINT",EDGE,{"disambiguationData":[TD([[subQ4,-1.0]])],"derivedFrom":subQ3}),1.0]])]});}
            var Q12;
            {var subQ6=sQuery(id+"F6.wireOp",EDGE,"E305");Q12=makeQuery(id+"F6.imprint","IMPRINT",FACE,{"disambiguationData":[TD([[makeQuery(id+"F6.imprint","IMPRINT",EDGE,{"derivedFrom":subQ6}),-1.0]])]});}
            var Q13;
            {var subQ0=sQuery(id+"F6.wireOp",EDGE,"E367");var subQ1=sQuery(id+"F6.wireOp",EDGE,"E277");var subQ2=makeQuery(id+"F6.imprint","INTERSECT",VERTEX,{"derivedFrom":[subQ1,subQ0]});Q13=makeQuery(id+"F6.imprint","IMPRINT",FACE,{"disambiguationData":[TD([[makeQuery(id+"F6.imprint","IMPRINT",EDGE,{"disambiguationData":[TD([[subQ2,-1.0]])],"derivedFrom":subQ1}),-1.0]])]});}
            var Q14;
            {var subQ0=sQuery(id+"F6.wireOp",EDGE,"E367");var subQ3=sQuery(id+"F6.wireOp",EDGE,"E280");var subQ4=makeQuery(id+"F6.imprint","INTERSECT",VERTEX,{"derivedFrom":[subQ3,subQ0]});Q14=makeQuery(id+"F6.imprint","IMPRINT",FACE,{"disambiguationData":[TD([[makeQuery(id+"F6.imprint","IMPRINT",EDGE,{"disambiguationData":[TD([[subQ4,-1.0]])],"derivedFrom":subQ3}),1.0]])]});}
            var Q15;
            {var subQ0=sQuery(id+"F6.wireOp",EDGE,"E278");Q15=makeQuery(id+"F6.imprint","IMPRINT",FACE,{"disambiguationData":[TD([[makeQuery(id+"F6.imprint","IMPRINT",EDGE,{"derivedFrom":subQ0}),-1.0]])]});}
            var Q16;
            {var subQ5=sQuery(id+"F6.wireOp",EDGE,"E280");var subQ6=sQuery(id+"F6.wireOp",EDGE,"E279");var subQ7=makeQuery(id+"F6.imprint","INTERSECT",VERTEX,{"derivedFrom":[subQ6,subQ5]});Q16=makeQuery(id+"F6.imprint","IMPRINT",FACE,{"disambiguationData":[TD([[makeQuery(id+"F6.imprint","IMPRINT",EDGE,{"disambiguationData":[TD([[subQ7,-1.0]])],"derivedFrom":subQ6}),-1.0]])]});}
            var Q17;
            {var subQ0=sQuery(id+"F6.wireOp",EDGE,"E369");var subQ1=sQuery(id+"F6.wireOp",EDGE,"E279");var subQ2=makeQuery(id+"F6.imprint","INTERSECT",VERTEX,{"derivedFrom":[subQ1,subQ0]});Q17=makeQuery(id+"F6.imprint","IMPRINT",FACE,{"disambiguationData":[TD([[makeQuery(id+"F6.imprint","IMPRINT",EDGE,{"disambiguationData":[TD([[subQ2,-1.0]])],"derivedFrom":subQ1}),1.0]])]});}
            var Q18;
            {var subQ0=sQuery(id+"F6.wireOp",EDGE,"E351");Q18=makeQuery(id+"F6.imprint","IMPRINT",FACE,{"disambiguationData":[TD([[makeQuery(id+"F6.imprint","IMPRINT",EDGE,{"derivedFrom":subQ0}),1.0]])]});}
            var Q19;
            {var subQ0=sQuery(id+"F6.wireOp",EDGE,"E383");var subQ1=sQuery(id+"F6.wireOp",EDGE,"E299");var subQ2=makeQuery(id+"F6.imprint","INTERSECT",VERTEX,{"derivedFrom":[subQ1,subQ0]});Q19=makeQuery(id+"F6.imprint","IMPRINT",FACE,{"disambiguationData":[TD([[makeQuery(id+"F6.imprint","IMPRINT",EDGE,{"disambiguationData":[TD([[subQ2,-1.0]])],"derivedFrom":subQ0}),1.0]])]});}
            var Q20;
            {var subQ5=sQuery(id+"F6.wireOp",EDGE,"E277");var subQ7=sQuery(id+"F6.wireOp",EDGE,"E375");var subQ9=makeQuery(id+"F6.imprint","INTERSECT",VERTEX,{"derivedFrom":[subQ5,subQ7]});Q20=makeQuery(id+"F6.imprint","IMPRINT",FACE,{"disambiguationData":[TD([[makeQuery(id+"F6.imprint","IMPRINT",EDGE,{"disambiguationData":[TD([[subQ9,-1.0]])],"derivedFrom":subQ5}),1.0]])]});}
            var Q21;
            {var subQ5=sQuery(id+"F6.wireOp",EDGE,"E379");var subQ6=sQuery(id+"F6.wireOp",EDGE,"E345");var subQ7=makeQuery(id+"F6.imprint","INTERSECT",VERTEX,{"derivedFrom":[subQ6,subQ5]});Q21=makeQuery(id+"F6.imprint","IMPRINT",FACE,{"disambiguationData":[TD([[makeQuery(id+"F6.imprint","IMPRINT",EDGE,{"disambiguationData":[TD([[subQ7,1.0]])],"derivedFrom":subQ6}),1.0]])]});}
            var Q22;
            {var subQ5=sQuery(id+"F6.wireOp",EDGE,"E385");Q22=makeQuery(id+"F6.imprint","IMPRINT",FACE,{"disambiguationData":[TD([[makeQuery(id+"F6.imprint","IMPRINT",EDGE,{"derivedFrom":subQ5}),-1.0]])]});}
            var Q23;
            {var subQ5=sQuery(id+"F6.wireOp",EDGE,"E386");Q23=makeQuery(id+"F6.imprint","IMPRINT",FACE,{"disambiguationData":[TD([[makeQuery(id+"F6.imprint","IMPRINT",EDGE,{"derivedFrom":subQ5}),1.0]])]});}
            var Q24;
            {var subQ11=sQuery(id+"F6.wireOp",EDGE,"E390");Q24=makeQuery(id+"F6.imprint","IMPRINT",FACE,{"disambiguationData":[TD([[makeQuery(id+"F6.imprint","IMPRINT",EDGE,{"derivedFrom":subQ11}),1.0]])]});}
            var Q25;
            {var subQ5=sQuery(id+"F6.wireOp",EDGE,"E389");Q25=makeQuery(id+"F6.imprint","IMPRINT",FACE,{"disambiguationData":[TD([[makeQuery(id+"F6.imprint","IMPRINT",EDGE,{"derivedFrom":subQ5}),-1.0]])]});}
            var Q26;
            {var subQ1=sQuery(id+"F6.wireOp",EDGE,"E393");var subQ3=sQuery(id+"F6.wireOp",EDGE,"E397");var subQ4=makeQuery(id+"F6.imprint","INTERSECT",VERTEX,{"derivedFrom":[subQ1,subQ3]});Q26=makeQuery(id+"F6.imprint","IMPRINT",FACE,{"disambiguationData":[TD([[makeQuery(id+"F6.imprint","IMPRINT",EDGE,{"disambiguationData":[TD([[subQ4,1.0]])],"derivedFrom":subQ1}),-1.0]])]});}
            var Q27;
            {var subQ0=sQuery(id+"F6.wireOp",EDGE,"E400");var subQ1=sQuery(id+"F6.wireOp",EDGE,"E394");var subQ2=makeQuery(id+"F6.imprint","INTERSECT",VERTEX,{"derivedFrom":[subQ1,subQ0]});Q27=makeQuery(id+"F6.imprint","IMPRINT",FACE,{"disambiguationData":[TD([[makeQuery(id+"F6.imprint","IMPRINT",EDGE,{"disambiguationData":[TD([[subQ2,-1.0]])],"derivedFrom":subQ1}),1.0]])]});}
            var Q28;
            {var subQ0=sQuery(id+"F6.wireOp",EDGE,"E400");var subQ1=sQuery(id+"F6.wireOp",EDGE,"E321");var subQ2=makeQuery(id+"F6.imprint","INTERSECT",VERTEX,{"derivedFrom":[subQ1,subQ0]});Q28=makeQuery(id+"F6.imprint","IMPRINT",FACE,{"disambiguationData":[TD([[makeQuery(id+"F6.imprint","IMPRINT",EDGE,{"disambiguationData":[TD([[subQ2,1.0]])],"derivedFrom":subQ1}),-1.0]])]});}
            var Q29;
            {var subQ0=sQuery(id+"F6.wireOp",EDGE,"E435");var subQ1=sQuery(id+"F6.wireOp",EDGE,"E396");var subQ2=makeQuery(id+"F6.imprint","INTERSECT",VERTEX,{"derivedFrom":[subQ1,subQ0]});Q29=makeQuery(id+"F6.imprint","IMPRINT",FACE,{"disambiguationData":[TD([[makeQuery(id+"F6.imprint","IMPRINT",EDGE,{"disambiguationData":[TD([[subQ2,-1.0]])],"derivedFrom":subQ1}),-1.0]])]});}
            var Q30;
            {var subQ0=sQuery(id+"F6.wireOp",EDGE,"E309");var subQ1=sQuery(id+"F6.wireOp",EDGE,"E308");var subQ2=makeQuery(id+"F6.imprint","INTERSECT",VERTEX,{"derivedFrom":[subQ1,subQ0]});Q30=makeQuery(id+"F6.imprint","IMPRINT",FACE,{"disambiguationData":[TD([[makeQuery(id+"F6.imprint","IMPRINT",EDGE,{"disambiguationData":[TD([[subQ2,1.0]])],"derivedFrom":subQ1}),1.0]])]});}
            var Q31;
            {var subQ0=sQuery(id+"F6.wireOp",EDGE,"E395");var subQ1=sQuery(id+"F6.wireOp",EDGE,"E331");var subQ2=makeQuery(id+"F6.imprint","INTERSECT",VERTEX,{"derivedFrom":[subQ1,subQ0]});Q31=makeQuery(id+"F6.imprint","IMPRINT",FACE,{"disambiguationData":[TD([[makeQuery(id+"F6.imprint","IMPRINT",EDGE,{"disambiguationData":[TD([[subQ2,-1.0]])],"derivedFrom":subQ1}),1.0]])]});}
            var Q32;
            {var subQ1=sQuery(id+"F6.wireOp",EDGE,"E332");var subQ3=sQuery(id+"F6.wireOp",EDGE,"E400");var subQ4=makeQuery(id+"F6.imprint","INTERSECT",VERTEX,{"derivedFrom":[subQ1,subQ3]});Q32=makeQuery(id+"F6.imprint","IMPRINT",FACE,{"disambiguationData":[TD([[makeQuery(id+"F6.imprint","IMPRINT",EDGE,{"disambiguationData":[TD([[subQ4,1.0]])],"derivedFrom":subQ3}),-1.0]])]});}
            var Q33;
            {var subQ6=sQuery(id+"F6.wireOp",EDGE,"E322");var subQ9=sQuery(id+"F6.wireOp",EDGE,"E321");var subQ11=makeQuery(id+"F6.imprint","INTERSECT",VERTEX,{"derivedFrom":[subQ9,subQ6]});Q33=makeQuery(id+"F6.imprint","IMPRINT",FACE,{"disambiguationData":[TD([[makeQuery(id+"F6.imprint","IMPRINT",EDGE,{"disambiguationData":[TD([[subQ11,-1.0]])],"derivedFrom":subQ9}),-1.0]])]});}
            var Q34;
            {var subQ1=sQuery(id+"F6.wireOp",EDGE,"E330");var subQ3=sQuery(id+"F6.wireOp",EDGE,"E401");var subQ4=makeQuery(id+"F6.imprint","INTERSECT",VERTEX,{"derivedFrom":[subQ1,subQ3]});Q34=makeQuery(id+"F6.imprint","IMPRINT",FACE,{"disambiguationData":[TD([[makeQuery(id+"F6.imprint","IMPRINT",EDGE,{"disambiguationData":[TD([[subQ4,1.0]])],"derivedFrom":subQ3}),1.0]])]});}
            var Q35;
            {var subQ1=sQuery(id+"F6.wireOp",EDGE,"E433");var subQ5=sQuery(id+"F6.wireOp",EDGE,"E432");var subQ6=makeQuery(id+"F6.imprint","INTERSECT",VERTEX,{"derivedFrom":[subQ5,subQ1]});Q35=makeQuery(id+"F6.imprint","IMPRINT",FACE,{"disambiguationData":[TD([[makeQuery(id+"F6.imprint","IMPRINT",EDGE,{"disambiguationData":[TD([[subQ6,-1.0]])],"derivedFrom":subQ1}),-1.0]])]});}
            var Q36;
            {var subQ0=sQuery(id+"F6.wireOp",EDGE,"E433");var subQ1=sQuery(id+"F6.wireOp",EDGE,"E309");var subQ2=makeQuery(id+"F6.imprint","INTERSECT",VERTEX,{"derivedFrom":[subQ1,subQ0]});Q36=makeQuery(id+"F6.imprint","IMPRINT",FACE,{"disambiguationData":[TD([[makeQuery(id+"F6.imprint","IMPRINT",EDGE,{"disambiguationData":[TD([[subQ2,-1.0]])],"derivedFrom":subQ1}),1.0]])]});}
            var Q37;
            {var subQ0=sQuery(id+"F6.wireOp",EDGE,"E429");Q37=makeQuery(id+"F6.imprint","IMPRINT",FACE,{"disambiguationData":[TD([[makeQuery(id+"F6.imprint","IMPRINT",EDGE,{"derivedFrom":subQ0}),-1.0]])]});}
            var Q38;
            {var subQ0=sQuery(id+"F6.wireOp",EDGE,"E430");Q38=makeQuery(id+"F6.imprint","IMPRINT",FACE,{"disambiguationData":[TD([[makeQuery(id+"F6.imprint","IMPRINT",EDGE,{"derivedFrom":subQ0}),1.0]])]});}
            var Q39;
            {var subQ2=sQuery(id+"F6.wireOp",EDGE,"E426");Q39=makeQuery(id+"F6.imprint","IMPRINT",FACE,{"disambiguationData":[TD([[makeQuery(id+"F6.imprint","IMPRINT",EDGE,{"derivedFrom":subQ2}),1.0]])]});}
            var Q40;
            {var subQ0=sQuery(id+"F6.wireOp",EDGE,"E425");Q40=makeQuery(id+"F6.imprint","IMPRINT",FACE,{"disambiguationData":[TD([[makeQuery(id+"F6.imprint","IMPRINT",EDGE,{"derivedFrom":subQ0}),1.0]])]});}
            var Q41;
            {var subQ0=sQuery(id+"F6.wireOp",EDGE,"E312");var subQ1=sQuery(id+"F6.wireOp",EDGE,"E311");var subQ2=makeQuery(id+"F6.imprint","INTERSECT",VERTEX,{"derivedFrom":[subQ1,subQ0]});Q41=makeQuery(id+"F6.imprint","IMPRINT",FACE,{"disambiguationData":[TD([[makeQuery(id+"F6.imprint","IMPRINT",EDGE,{"disambiguationData":[TD([[subQ2,-1.0]])],"derivedFrom":subQ1}),-1.0]])]});}
            var Q42;
            {var subQ1=sQuery(id+"F6.wireOp",EDGE,"E317");var subQ3=makeQuery(id+"F6.imprint","INTERSECT",VERTEX,{"derivedFrom":[subQ1,sQuery(id+"F6.wireOp",EDGE,"E325")]});Q42=makeQuery(id+"F6.imprint","IMPRINT",FACE,{"disambiguationData":[TD([[makeQuery(id+"F6.imprint","IMPRINT",EDGE,{"disambiguationData":[TD([[subQ3,1.0]])],"derivedFrom":subQ1}),1.0]])]});}
            var Q43;
            {var subQ0=sQuery(id+"F6.wireOp",EDGE,"E403");var subQ1=sQuery(id+"F6.wireOp",EDGE,"E322");var subQ2=makeQuery(id+"F6.imprint","INTERSECT",VERTEX,{"derivedFrom":[subQ1,subQ0]});Q43=makeQuery(id+"F6.imprint","IMPRINT",FACE,{"disambiguationData":[TD([[makeQuery(id+"F6.imprint","IMPRINT",EDGE,{"disambiguationData":[TD([[subQ2,-1.0]])],"derivedFrom":subQ1}),1.0]])]});}
            var Q44;
            {var subQ0=sQuery(id+"F6.wireOp",EDGE,"E404");var subQ1=sQuery(id+"F6.wireOp",EDGE,"E330");var subQ2=makeQuery(id+"F6.imprint","INTERSECT",VERTEX,{"derivedFrom":[subQ1,subQ0]});Q44=makeQuery(id+"F6.imprint","IMPRINT",FACE,{"disambiguationData":[TD([[makeQuery(id+"F6.imprint","IMPRINT",EDGE,{"disambiguationData":[TD([[subQ2,-1.0]])],"derivedFrom":subQ1}),1.0]])]});}
            var Q45;
            {var subQ3=sQuery(id+"F6.wireOp",EDGE,"E406");Q45=makeQuery(id+"F6.imprint","IMPRINT",FACE,{"disambiguationData":[TD([[makeQuery(id+"F6.imprint","IMPRINT",EDGE,{"derivedFrom":subQ3}),-1.0]])]});}
            var Q46;
            {var subQ4=sQuery(id+"F6.wireOp",EDGE,"E407");Q46=makeQuery(id+"F6.imprint","IMPRINT",FACE,{"disambiguationData":[TD([[makeQuery(id+"F6.imprint","IMPRINT",EDGE,{"derivedFrom":subQ4}),-1.0]])]});}
            var Q47;
            {var subQ0=sQuery(id+"F6.wireOp",EDGE,"E325");var subQ1=sQuery(id+"F6.wireOp",EDGE,"E324");var subQ2=makeQuery(id+"F6.imprint","INTERSECT",VERTEX,{"derivedFrom":[subQ1,subQ0]});Q47=makeQuery(id+"F6.imprint","IMPRINT",FACE,{"disambiguationData":[TD([[makeQuery(id+"F6.imprint","IMPRINT",EDGE,{"disambiguationData":[TD([[subQ2,-1.0]])],"derivedFrom":subQ1}),-1.0]])]});}
            var Q48;
            {var subQ0=sQuery(id+"F6.wireOp",EDGE,"E410");var subQ1=sQuery(id+"F6.wireOp",EDGE,"E329");var subQ2=makeQuery(id+"F6.imprint","INTERSECT",VERTEX,{"derivedFrom":[subQ1,subQ0]});Q48=makeQuery(id+"F6.imprint","IMPRINT",FACE,{"disambiguationData":[TD([[makeQuery(id+"F6.imprint","IMPRINT",EDGE,{"disambiguationData":[TD([[subQ2,-1.0]])],"derivedFrom":subQ1}),1.0]])]});}
            var Q49;
            {var subQ3=sQuery(id+"F6.wireOp",EDGE,"E412");Q49=makeQuery(id+"F6.imprint","IMPRINT",FACE,{"disambiguationData":[TD([[makeQuery(id+"F6.imprint","IMPRINT",EDGE,{"derivedFrom":subQ3}),1.0]])]});}
            var Q50;
            {var subQ0=sQuery(id+"F6.wireOp",EDGE,"E413");var subQ1=sQuery(id+"F6.wireOp",EDGE,"E329");var subQ2=makeQuery(id+"F6.imprint","INTERSECT",VERTEX,{"derivedFrom":[subQ1,subQ0]});Q50=makeQuery(id+"F6.imprint","IMPRINT",FACE,{"disambiguationData":[TD([[makeQuery(id+"F6.imprint","IMPRINT",EDGE,{"disambiguationData":[TD([[subQ2,-1.0]])],"derivedFrom":subQ1}),1.0]])]});}
            var Q51;
            {var subQ0=sQuery(id+"F6.wireOp",EDGE,"E316");var subQ1=makeQuery(id+"F6.imprint","INTERSECT",VERTEX,{"derivedFrom":[subQ0,sQuery(id+"F6.wireOp",EDGE,"E414")]});Q51=makeQuery(id+"F6.imprint","IMPRINT",FACE,{"disambiguationData":[TD([[makeQuery(id+"F6.imprint","IMPRINT",EDGE,{"disambiguationData":[TD([[subQ1,-1.0]])],"derivedFrom":subQ0}),1.0]])]});}
            var Q52;
            {var subQ1=sQuery(id+"F6.wireOp",EDGE,"E312");var subQ3=sQuery(id+"F6.wireOp",EDGE,"E421");var subQ4=makeQuery(id+"F6.imprint","INTERSECT",VERTEX,{"derivedFrom":[subQ1,subQ3]});Q52=makeQuery(id+"F6.imprint","IMPRINT",FACE,{"disambiguationData":[TD([[makeQuery(id+"F6.imprint","IMPRINT",EDGE,{"disambiguationData":[TD([[subQ4,-1.0]])],"derivedFrom":subQ3}),-1.0]])]});}
            var Q53;
            {var subQ3=sQuery(id+"F6.wireOp",EDGE,"E415");Q53=makeQuery(id+"F6.imprint","IMPRINT",FACE,{"disambiguationData":[TD([[makeQuery(id+"F6.imprint","IMPRINT",EDGE,{"derivedFrom":subQ3}),-1.0]])]});}
            var Q54;
            {var subQ3=sQuery(id+"F6.wireOp",EDGE,"E419");Q54=makeQuery(id+"F6.imprint","IMPRINT",FACE,{"disambiguationData":[TD([[makeQuery(id+"F6.imprint","IMPRINT",EDGE,{"derivedFrom":subQ3}),1.0]])]});}
            var Q55;
            {var subQ0=sQuery(id+"F6.wireOp",EDGE,"E417");Q55=makeQuery(id+"F6.imprint","IMPRINT",FACE,{"disambiguationData":[TD([[makeQuery(id+"F6.imprint","IMPRINT",EDGE,{"derivedFrom":subQ0}),1.0]])]});}
            extrude(context, id + "F14", {"entities" : qUnion([Q0, Q1, Q2, Q3, Q4, Q5, Q6, Q7, Q8, Q9, Q10, Q11, Q12, Q13, Q14, Q15, Q16, Q17, Q18, Q19, Q20, Q21, Q22, Q23, Q24, Q25, Q26, Q27, Q28, Q29, Q30, Q31, Q32, Q33, Q34, Q35, Q36, Q37, Q38, Q39, Q40, Q41, Q42, Q43, Q44, Q45, Q46, Q47, Q48, Q49, Q50, Q51, Q52, Q53, Q54, Q55]), "depth" : 7.75 * mm, "offsetDistance" : 25 * mm});
        }
        {
            var Q0;
            Q0 = qSketchRegion(id + "F2", true);
            extrude(context, id + "F15", {"entities" : qUnion([Q0]), "depth" : 7 * mm, "offsetDistance" : 25 * mm});
        }
    });
